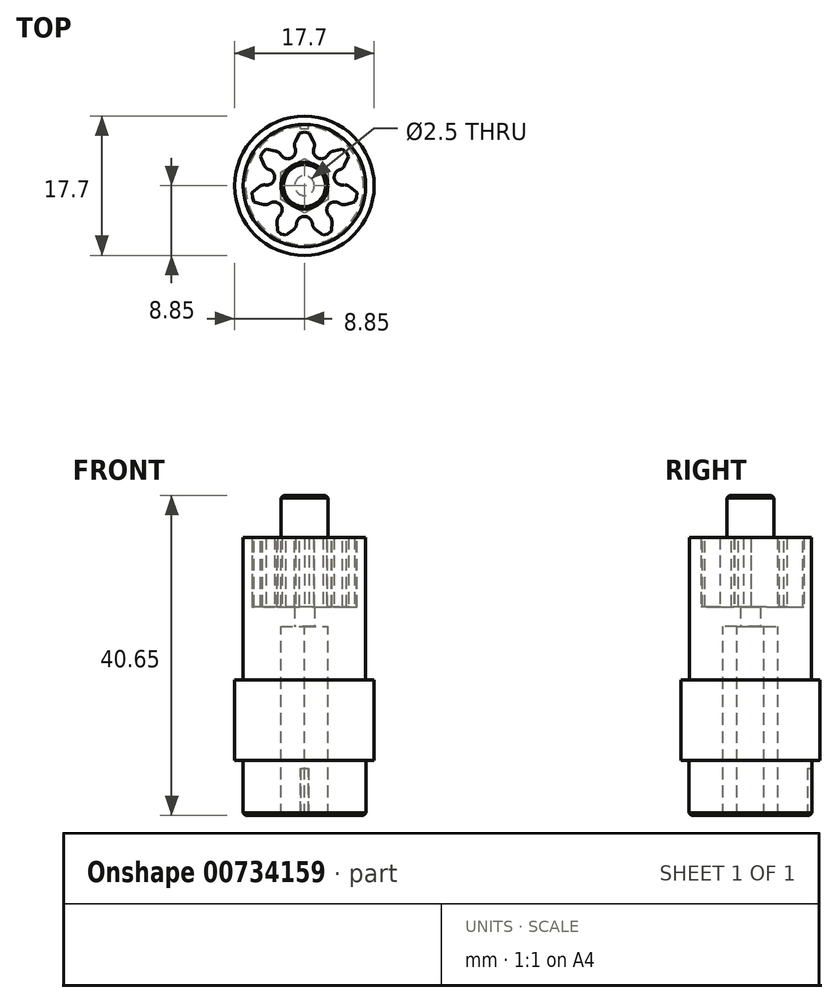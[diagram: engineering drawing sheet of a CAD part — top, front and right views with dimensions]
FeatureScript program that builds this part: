
annotation { "Feature Type Name" : "Feature", "Feature Type Description" : "" }
export const myFeature = defineFeature(function(context is Context, id is Id, definition is map)
    precondition{}
    {
        {
            var Q0;
            Q0=qCreatedBy(makeId("Top.planeOp"),FACE);
            var sketch = newSketch(context, id + "F0", { "sketchPlane" : qUnion([Q0])});
            skCircle(sketch, "E0", {"center": v(0, 0) * mm, "radius": 7.77 * mm});
            skCircle(sketch, "E1.cCircle", {"center": v(0, 0) * mm, "radius": 3 * mm, "construction": true});
            skLineSegment(sketch, "E1.0", {"start": v(0, 3.46) * mm, "end": v(3, 1.73) * mm});
            skLineSegment(sketch, "E1.1", {"start": v(3, 1.73) * mm, "end": v(3, -1.73) * mm});
            skLineSegment(sketch, "E1.2", {"start": v(3, -1.73) * mm, "end": v(0, -3.46) * mm});
            skLineSegment(sketch, "E1.3", {"start": v(0, -3.46) * mm, "end": v(-3, -1.73) * mm});
            skLineSegment(sketch, "E1.4", {"start": v(-3, -1.73) * mm, "end": v(-3, 1.73) * mm});
            skLineSegment(sketch, "E1.5", {"start": v(-3, 1.73) * mm, "end": v(0, 3.46) * mm});
            skPoint(sketch, "E1.0.midPoint", {"position": v(1.5, 2.6) * mm});
            skCircle(sketch, "E2", {"center": v(0, 0) * mm, "radius": 1.25 * mm});
            skSolve(sketch);
        }
        {
            var Q0;
            Q0=makeQuery(id+"F0.imprint","IMPRINT",FACE,{"disambiguationData":[TD([[makeQuery(id+"F0.imprint","IMPRINT",EDGE,{"derivedFrom":sQuery(id+"F0.wireOp",EDGE,"E1.0")}),-1.0]])]});
            var Q1;
            Q1=makeQuery(id+"F0.imprint","IMPRINT",FACE,{"disambiguationData":[TD([[makeQuery(id+"F0.imprint","IMPRINT",EDGE,{"derivedFrom":sQuery(id+"F0.wireOp",EDGE,"E0")}),1.0]])]});
            extrude(context, id + "F1", {"entities" : qUnion([Q0, Q1]), "depth" : 2.5 * mm, "offsetDistance" : 25 * mm});
        }
        {
            var Q0;
            Q0=makeQuery(id+"F0.imprint","IMPRINT",FACE,{"disambiguationData":[TD([[makeQuery(id+"F0.imprint","IMPRINT",EDGE,{"derivedFrom":sQuery(id+"F0.wireOp",EDGE,"E0")}),1.0]])]});
            extrude(context, id + "F2", {"entities" : qUnion([Q0]), "operationType" : NewBodyOperationType.ADD, "oppositeDirection" : true, "depth" : 6.8 * mm, "offsetDistance" : 25 * mm});
        }
        {
            var Q0;
            Q0=makeQuery(id+"F2.opExtrude","CAP_FACE",FACE,{"disambiguationData":[OSD([sQuery(id+"F0.wireOp",EDGE,"E0"),sQuery(id+"F0.wireOp",EDGE,"E1.0"),sQuery(id+"F0.wireOp",EDGE,"E1.1"),sQuery(id+"F0.wireOp",EDGE,"E1.2"),sQuery(id+"F0.wireOp",EDGE,"E1.3"),sQuery(id+"F0.wireOp",EDGE,"E1.4"),sQuery(id+"F0.wireOp",EDGE,"E1.5")])],"isStart":false});
            var sketch = newSketch(context, id + "F3", { "sketchPlane" : qUnion([Q0])});
            skCircle(sketch, "E3", {"center": v(0, 0) * mm, "radius": 8.85 * mm});
            skSolve(sketch);
        }
        {
            var Q0;
            Q0=makeQuery(id+"F3.imprint","IMPRINT",FACE,{"disambiguationData":[TD([[makeQuery(id+"F3.imprint","IMPRINT",EDGE,{"derivedFrom":makeQuery(id+"F2.opExtrude","CAP_EDGE",EDGE,{"disambiguationData":[OSD([sQuery(id+"F0.wireOp",EDGE,"E0")])],"isStart":false})}),-1.0]])]});
            var Q1;
            Q1=makeQuery(id+"F3.imprint","IMPRINT",FACE,{"disambiguationData":[TD([[makeQuery(id+"F3.imprint","IMPRINT",EDGE,{"derivedFrom":sQuery(id+"F3.wireOp",EDGE,"E3")}),1.0]])]});
            extrude(context, id + "F4", {"entities" : qUnion([Q0, Q1]), "operationType" : NewBodyOperationType.ADD, "depth" : 1.5 * mm, "offsetDistance" : 25 * mm});
        }
        {
            var Q0;
            Q0=makeQuery(id+"F4.opExtrude","CAP_FACE",FACE,{"disambiguationData":[OSD([sQuery(id+"F0.wireOp",EDGE,"E1.0"),sQuery(id+"F0.wireOp",EDGE,"E1.1"),sQuery(id+"F0.wireOp",EDGE,"E1.2"),sQuery(id+"F0.wireOp",EDGE,"E1.3"),sQuery(id+"F0.wireOp",EDGE,"E1.4"),sQuery(id+"F0.wireOp",EDGE,"E1.5"),sQuery(id+"F3.wireOp",EDGE,"E3")])],"isStart":false});
            var sketch = newSketch(context, id + "F5", { "sketchPlane" : qUnion([Q0])});
            skCircle(sketch, "E4", {"center": v(0, 0) * mm, "radius": 16.2 * mm, "construction": true});
            skLineSegment(sketch, "E5", {"start": v(0, 0) * mm, "end": v(0, 17.55) * mm, "construction": true});
            skCircle(sketch, "E6", {"center": v(0, 0) * mm, "radius": 15.75 * mm, "construction": true});
            skCircle(sketch, "E7", {"center": v(0, 0) * mm, "radius": 17.55 * mm, "construction": true});
            skArc(sketch, "E8", {"start": v(-0.72, 16.18) * mm, "mid": v(-1.14, 15.7) * mm, "end": v(-1.62, 16.12) * mm});
            skArc(sketch, "E9", {"start": v(-0.3, 17.55) * mm, "mid": v(-0.15, 17.55) * mm, "end": v(0, 17.55) * mm});
            skLineSegment(sketch, "E10", {"start": v(-0.72, 16.18) * mm, "end": v(-0.74, 16.43) * mm});
            skLineSegment(sketch, "E11", {"start": v(-0.74, 16.43) * mm, "end": v(-0.3, 17.55) * mm});
            skArc(sketch, "E12.MirrorCS", {"start": v(0.3, 17.55) * mm, "mid": v(0.15, 17.55) * mm, "end": v(0, 17.55) * mm});
            skLineSegment(sketch, "E13.MirrorCS", {"start": v(0.74, 16.43) * mm, "end": v(0.3, 17.55) * mm});
            skLineSegment(sketch, "E14.MirrorCS", {"start": v(0.72, 16.18) * mm, "end": v(0.74, 16.43) * mm});
            skArc(sketch, "E15.1.0", {"start": v(-2.24, 17.4) * mm, "mid": v(-2.39, 17.39) * mm, "end": v(-2.53, 17.37) * mm});
            skArc(sketch, "E15.1.1", {"start": v(-2.83, 17.32) * mm, "mid": v(-2.68, 17.34) * mm, "end": v(-2.53, 17.37) * mm});
            skLineSegment(sketch, "E15.1.2", {"start": v(-1.64, 16.37) * mm, "end": v(-2.24, 17.4) * mm});
            skLineSegment(sketch, "E15.1.3", {"start": v(-1.62, 16.12) * mm, "end": v(-1.64, 16.37) * mm});
            skLineSegment(sketch, "E15.1.4", {"start": v(-3.1, 16.15) * mm, "end": v(-2.83, 17.32) * mm});
            skLineSegment(sketch, "E15.1.5", {"start": v(-3.05, 15.9) * mm, "end": v(-3.1, 16.15) * mm});
            skArc(sketch, "E15.1.6", {"start": v(-3.05, 15.9) * mm, "mid": v(-3.4, 15.38) * mm, "end": v(-3.93, 15.71) * mm});
            skArc(sketch, "E15.2.0", {"start": v(-4.73, 16.9) * mm, "mid": v(-4.87, 16.86) * mm, "end": v(-5.01, 16.81) * mm});
            skArc(sketch, "E15.2.1", {"start": v(-5.3, 16.72) * mm, "mid": v(-5.16, 16.77) * mm, "end": v(-5.01, 16.81) * mm});
            skLineSegment(sketch, "E15.2.2", {"start": v(-3.99, 15.96) * mm, "end": v(-4.73, 16.9) * mm});
            skLineSegment(sketch, "E15.2.3", {"start": v(-3.93, 15.71) * mm, "end": v(-3.99, 15.96) * mm});
            skLineSegment(sketch, "E15.2.4", {"start": v(-5.4, 15.53) * mm, "end": v(-5.3, 16.72) * mm});
            skLineSegment(sketch, "E15.2.5", {"start": v(-5.31, 15.3) * mm, "end": v(-5.4, 15.53) * mm});
            skArc(sketch, "E15.2.6", {"start": v(-5.31, 15.3) * mm, "mid": v(-5.57, 14.72) * mm, "end": v(-6.15, 14.98) * mm});
            skArc(sketch, "E15.3.0", {"start": v(-7.11, 16.03) * mm, "mid": v(-7.25, 15.97) * mm, "end": v(-7.39, 15.9) * mm});
            skArc(sketch, "E15.3.1", {"start": v(-7.66, 15.78) * mm, "mid": v(-7.52, 15.84) * mm, "end": v(-7.39, 15.9) * mm});
            skLineSegment(sketch, "E15.3.2", {"start": v(-6.24, 15.2) * mm, "end": v(-7.11, 16.03) * mm});
            skLineSegment(sketch, "E15.3.3", {"start": v(-6.15, 14.98) * mm, "end": v(-6.24, 15.2) * mm});
            skLineSegment(sketch, "E15.3.4", {"start": v(-7.58, 14.58) * mm, "end": v(-7.66, 15.78) * mm});
            skLineSegment(sketch, "E15.3.5", {"start": v(-7.46, 14.36) * mm, "end": v(-7.58, 14.58) * mm});
            skArc(sketch, "E15.3.6", {"start": v(-7.46, 14.36) * mm, "mid": v(-7.64, 13.76) * mm, "end": v(-8.25, 13.92) * mm});
            skArc(sketch, "E15.4.0", {"start": v(-9.35, 14.83) * mm, "mid": v(-9.48, 14.75) * mm, "end": v(-9.6, 14.66) * mm});
            skArc(sketch, "E15.4.1", {"start": v(-9.85, 14.5) * mm, "mid": v(-9.73, 14.58) * mm, "end": v(-9.6, 14.66) * mm});
            skLineSegment(sketch, "E15.4.2", {"start": v(-8.37, 14.14) * mm, "end": v(-9.35, 14.83) * mm});
            skLineSegment(sketch, "E15.4.3", {"start": v(-8.25, 13.92) * mm, "end": v(-8.37, 14.14) * mm});
            skLineSegment(sketch, "E15.4.4", {"start": v(-9.6, 13.33) * mm, "end": v(-9.85, 14.5) * mm});
            skLineSegment(sketch, "E15.4.5", {"start": v(-9.45, 13.13) * mm, "end": v(-9.6, 13.33) * mm});
            skArc(sketch, "E15.4.6", {"start": v(-9.45, 13.13) * mm, "mid": v(-9.54, 12.5) * mm, "end": v(-10.16, 12.58) * mm});
            skArc(sketch, "E15.5.0", {"start": v(-11.39, 13.3) * mm, "mid": v(-11.5, 13.21) * mm, "end": v(-11.61, 13.11) * mm});
            skArc(sketch, "E15.5.1", {"start": v(-11.83, 12.9) * mm, "mid": v(-11.72, 13.01) * mm, "end": v(-11.61, 13.11) * mm});
            skLineSegment(sketch, "E15.5.2", {"start": v(-10.32, 12.77) * mm, "end": v(-11.39, 13.3) * mm});
            skLineSegment(sketch, "E15.5.3", {"start": v(-10.16, 12.58) * mm, "end": v(-10.32, 12.77) * mm});
            skLineSegment(sketch, "E15.5.4", {"start": v(-11.42, 11.79) * mm, "end": v(-11.83, 12.9) * mm});
            skLineSegment(sketch, "E15.5.5", {"start": v(-11.24, 11.61) * mm, "end": v(-11.42, 11.79) * mm});
            skArc(sketch, "E15.5.6", {"start": v(-11.24, 11.61) * mm, "mid": v(-11.23, 10.98) * mm, "end": v(-11.86, 10.96) * mm});
            skArc(sketch, "E15.6.0", {"start": v(-13.18, 11.51) * mm, "mid": v(-13.28, 11.4) * mm, "end": v(-13.38, 11.28) * mm});
            skArc(sketch, "E15.6.1", {"start": v(-13.57, 11.05) * mm, "mid": v(-13.47, 11.17) * mm, "end": v(-13.38, 11.28) * mm});
            skLineSegment(sketch, "E15.6.2", {"start": v(-12.05, 11.14) * mm, "end": v(-13.18, 11.51) * mm});
            skLineSegment(sketch, "E15.6.3", {"start": v(-11.86, 10.96) * mm, "end": v(-12.05, 11.14) * mm});
            skLineSegment(sketch, "E15.6.4", {"start": v(-12.99, 10) * mm, "end": v(-13.57, 11.05) * mm});
            skLineSegment(sketch, "E15.6.5", {"start": v(-12.79, 9.85) * mm, "end": v(-12.99, 10) * mm});
            skArc(sketch, "E15.6.6", {"start": v(-12.79, 9.85) * mm, "mid": v(-12.69, 9.23) * mm, "end": v(-13.31, 9.12) * mm});
            skArc(sketch, "E15.7.0", {"start": v(-14.7, 9.47) * mm, "mid": v(-14.78, 9.35) * mm, "end": v(-14.85, 9.22) * mm});
            skArc(sketch, "E15.7.1", {"start": v(-15, 8.96) * mm, "mid": v(-14.93, 9.09) * mm, "end": v(-14.85, 9.22) * mm});
            skLineSegment(sketch, "E15.7.2", {"start": v(-13.52, 9.27) * mm, "end": v(-14.7, 9.47) * mm});
            skLineSegment(sketch, "E15.7.3", {"start": v(-13.31, 9.12) * mm, "end": v(-13.52, 9.27) * mm});
            skLineSegment(sketch, "E15.7.4", {"start": v(-14.29, 8) * mm, "end": v(-15, 8.96) * mm});
            skLineSegment(sketch, "E15.7.5", {"start": v(-14.07, 7.89) * mm, "end": v(-14.29, 8) * mm});
            skArc(sketch, "E15.7.6", {"start": v(-14.07, 7.89) * mm, "mid": v(-13.88, 7.29) * mm, "end": v(-14.48, 7.09) * mm});
            skArc(sketch, "E15.8.0", {"start": v(-15.9, 7.23) * mm, "mid": v(-15.96, 7.1) * mm, "end": v(-16.02, 6.96) * mm});
            skArc(sketch, "E15.8.1", {"start": v(-16.13, 6.68) * mm, "mid": v(-16.08, 6.82) * mm, "end": v(-16.02, 6.96) * mm});
            skLineSegment(sketch, "E15.8.2", {"start": v(-14.7, 7.2) * mm, "end": v(-15.9, 7.23) * mm});
            skLineSegment(sketch, "E15.8.3", {"start": v(-14.48, 7.09) * mm, "end": v(-14.7, 7.2) * mm});
            skLineSegment(sketch, "E15.8.4", {"start": v(-15.28, 5.84) * mm, "end": v(-16.13, 6.68) * mm});
            skLineSegment(sketch, "E15.8.5", {"start": v(-15.04, 5.76) * mm, "end": v(-15.28, 5.84) * mm});
            skArc(sketch, "E15.8.6", {"start": v(-15.04, 5.76) * mm, "mid": v(-14.77, 5.2) * mm, "end": v(-15.33, 4.9) * mm});
            skArc(sketch, "E15.9.0", {"start": v(-16.76, 4.84) * mm, "mid": v(-16.8, 4.7) * mm, "end": v(-16.84, 4.55) * mm});
            skArc(sketch, "E15.9.1", {"start": v(-16.91, 4.26) * mm, "mid": v(-16.88, 4.4) * mm, "end": v(-16.84, 4.55) * mm});
            skLineSegment(sketch, "E15.9.2", {"start": v(-15.57, 4.99) * mm, "end": v(-16.76, 4.84) * mm});
            skLineSegment(sketch, "E15.9.3", {"start": v(-15.33, 4.9) * mm, "end": v(-15.57, 4.99) * mm});
            skLineSegment(sketch, "E15.9.4", {"start": v(-15.94, 3.56) * mm, "end": v(-16.91, 4.26) * mm});
            skLineSegment(sketch, "E15.9.5", {"start": v(-15.7, 3.51) * mm, "end": v(-15.94, 3.56) * mm});
            skArc(sketch, "E15.9.6", {"start": v(-15.7, 3.51) * mm, "mid": v(-15.34, 2.99) * mm, "end": v(-15.86, 2.63) * mm});
            skArc(sketch, "E15.10.0", {"start": v(-17.26, 2.35) * mm, "mid": v(-17.28, 2.2) * mm, "end": v(-17.3, 2.06) * mm});
            skArc(sketch, "E15.10.1", {"start": v(-17.33, 1.76) * mm, "mid": v(-17.32, 1.9) * mm, "end": v(-17.3, 2.06) * mm});
            skLineSegment(sketch, "E15.10.2", {"start": v(-16.1, 2.67) * mm, "end": v(-17.26, 2.35) * mm});
            skLineSegment(sketch, "E15.10.3", {"start": v(-15.86, 2.63) * mm, "end": v(-16.1, 2.67) * mm});
            skLineSegment(sketch, "E15.10.4", {"start": v(-16.27, 1.2) * mm, "end": v(-17.33, 1.76) * mm});
            skLineSegment(sketch, "E15.10.5", {"start": v(-16.02, 1.19) * mm, "end": v(-16.27, 1.2) * mm});
            skArc(sketch, "E15.10.6", {"start": v(-16.02, 1.19) * mm, "mid": v(-15.6, 0.72) * mm, "end": v(-16.05, 0.29) * mm});
            skArc(sketch, "E15.11.0", {"start": v(-17.4, -0.18) * mm, "mid": v(-17.4, -0.33) * mm, "end": v(-17.4, -0.48) * mm});
            skArc(sketch, "E15.11.1", {"start": v(-17.38, -0.78) * mm, "mid": v(-17.39, -0.63) * mm, "end": v(-17.4, -0.48) * mm});
            skLineSegment(sketch, "E15.11.2", {"start": v(-16.3, 0.3) * mm, "end": v(-17.4, -0.18) * mm});
            skLineSegment(sketch, "E15.11.3", {"start": v(-16.05, 0.29) * mm, "end": v(-16.3, 0.3) * mm});
            skLineSegment(sketch, "E15.11.4", {"start": v(-16.25, -1.18) * mm, "end": v(-17.38, -0.78) * mm});
            skLineSegment(sketch, "E15.11.5", {"start": v(-16, -1.15) * mm, "end": v(-16.25, -1.18) * mm});
            skArc(sketch, "E15.11.6", {"start": v(-16, -1.15) * mm, "mid": v(-15.51, -1.55) * mm, "end": v(-15.9, -2.05) * mm});
            skArc(sketch, "E15.12.0", {"start": v(-17.17, -2.71) * mm, "mid": v(-17.14, -2.86) * mm, "end": v(-17.12, -3) * mm});
            skArc(sketch, "E15.12.1", {"start": v(-17.06, -3.3) * mm, "mid": v(-17.09, -3.15) * mm, "end": v(-17.12, -3) * mm});
            skLineSegment(sketch, "E15.12.2", {"start": v(-16.15, -2.08) * mm, "end": v(-17.17, -2.71) * mm});
            skLineSegment(sketch, "E15.12.3", {"start": v(-15.9, -2.05) * mm, "end": v(-16.15, -2.08) * mm});
            skLineSegment(sketch, "E15.12.4", {"start": v(-15.88, -3.53) * mm, "end": v(-17.06, -3.3) * mm});
            skLineSegment(sketch, "E15.12.5", {"start": v(-15.64, -3.47) * mm, "end": v(-15.88, -3.53) * mm});
            skArc(sketch, "E15.12.6", {"start": v(-15.64, -3.47) * mm, "mid": v(-15.1, -3.8) * mm, "end": v(-15.41, -4.34) * mm});
            skArc(sketch, "E15.13.0", {"start": v(-16.57, -5.18) * mm, "mid": v(-16.52, -5.32) * mm, "end": v(-16.47, -5.46) * mm});
            skArc(sketch, "E15.13.1", {"start": v(-16.37, -5.75) * mm, "mid": v(-16.43, -5.6) * mm, "end": v(-16.47, -5.46) * mm});
            skLineSegment(sketch, "E15.13.2", {"start": v(-15.66, -4.4) * mm, "end": v(-16.57, -5.18) * mm});
            skLineSegment(sketch, "E15.13.3", {"start": v(-15.41, -4.34) * mm, "end": v(-15.66, -4.4) * mm});
            skLineSegment(sketch, "E15.13.4", {"start": v(-15.18, -5.8) * mm, "end": v(-16.37, -5.75) * mm});
            skLineSegment(sketch, "E15.13.5", {"start": v(-14.95, -5.7) * mm, "end": v(-15.18, -5.8) * mm});
            skArc(sketch, "E15.13.6", {"start": v(-14.95, -5.7) * mm, "mid": v(-14.36, -5.95) * mm, "end": v(-14.6, -6.54) * mm});
            skArc(sketch, "E15.14.0", {"start": v(-15.62, -7.54) * mm, "mid": v(-15.55, -7.67) * mm, "end": v(-15.48, -7.8) * mm});
            skArc(sketch, "E15.14.1", {"start": v(-15.34, -8.07) * mm, "mid": v(-15.41, -7.94) * mm, "end": v(-15.48, -7.8) * mm});
            skLineSegment(sketch, "E15.14.2", {"start": v(-14.83, -6.64) * mm, "end": v(-15.62, -7.54) * mm});
            skLineSegment(sketch, "E15.14.3", {"start": v(-14.6, -6.54) * mm, "end": v(-14.83, -6.64) * mm});
            skLineSegment(sketch, "E15.14.4", {"start": v(-14.15, -7.95) * mm, "end": v(-15.34, -8.07) * mm});
            skLineSegment(sketch, "E15.14.5", {"start": v(-13.94, -7.82) * mm, "end": v(-14.15, -7.95) * mm});
            skArc(sketch, "E15.14.6", {"start": v(-13.94, -7.82) * mm, "mid": v(-13.32, -7.97) * mm, "end": v(-13.47, -8.59) * mm});
            skArc(sketch, "E15.15.0", {"start": v(-14.33, -9.73) * mm, "mid": v(-14.25, -9.85) * mm, "end": v(-14.16, -9.97) * mm});
            skArc(sketch, "E15.15.1", {"start": v(-13.98, -10.21) * mm, "mid": v(-14.07, -10.1) * mm, "end": v(-14.16, -9.97) * mm});
            skLineSegment(sketch, "E15.15.2", {"start": v(-13.68, -8.72) * mm, "end": v(-14.33, -9.73) * mm});
            skLineSegment(sketch, "E15.15.3", {"start": v(-13.47, -8.59) * mm, "end": v(-13.68, -8.72) * mm});
            skLineSegment(sketch, "E15.15.4", {"start": v(-12.82, -9.92) * mm, "end": v(-13.98, -10.21) * mm});
            skLineSegment(sketch, "E15.15.5", {"start": v(-12.63, -9.76) * mm, "end": v(-12.82, -9.92) * mm});
            skArc(sketch, "E15.15.6", {"start": v(-12.63, -9.76) * mm, "mid": v(-12, -9.83) * mm, "end": v(-12.05, -10.46) * mm});
            skArc(sketch, "E15.16.0", {"start": v(-12.74, -11.7) * mm, "mid": v(-12.64, -11.82) * mm, "end": v(-12.53, -11.92) * mm});
            skArc(sketch, "E15.16.1", {"start": v(-12.32, -12.14) * mm, "mid": v(-12.43, -12.03) * mm, "end": v(-12.53, -11.92) * mm});
            skLineSegment(sketch, "E15.16.2", {"start": v(-12.24, -10.62) * mm, "end": v(-12.74, -11.7) * mm});
            skLineSegment(sketch, "E15.16.3", {"start": v(-12.05, -10.46) * mm, "end": v(-12.24, -10.62) * mm});
            skLineSegment(sketch, "E15.16.4", {"start": v(-11.22, -11.68) * mm, "end": v(-12.32, -12.14) * mm});
            skLineSegment(sketch, "E15.16.5", {"start": v(-11.05, -11.5) * mm, "end": v(-11.22, -11.68) * mm});
            skArc(sketch, "E15.16.6", {"start": v(-11.05, -11.5) * mm, "mid": v(-10.42, -11.47) * mm, "end": v(-10.38, -12.1) * mm});
            skArc(sketch, "E15.17.0", {"start": v(-10.88, -13.44) * mm, "mid": v(-10.76, -13.53) * mm, "end": v(-10.64, -13.62) * mm});
            skArc(sketch, "E15.17.1", {"start": v(-10.4, -13.8) * mm, "mid": v(-10.52, -13.71) * mm, "end": v(-10.64, -13.62) * mm});
            skLineSegment(sketch, "E15.17.2", {"start": v(-10.54, -12.29) * mm, "end": v(-10.88, -13.44) * mm});
            skLineSegment(sketch, "E15.17.3", {"start": v(-10.38, -12.1) * mm, "end": v(-10.54, -12.29) * mm});
            skLineSegment(sketch, "E15.17.4", {"start": v(-9.38, -13.19) * mm, "end": v(-10.4, -13.8) * mm});
            skLineSegment(sketch, "E15.17.5", {"start": v(-9.24, -12.98) * mm, "end": v(-9.38, -13.19) * mm});
            skArc(sketch, "E15.17.6", {"start": v(-9.24, -12.98) * mm, "mid": v(-8.62, -12.86) * mm, "end": v(-8.49, -13.48) * mm});
            skArc(sketch, "E15.18.0", {"start": v(-8.78, -14.87) * mm, "mid": v(-8.65, -14.95) * mm, "end": v(-8.52, -15.02) * mm});
            skArc(sketch, "E15.18.1", {"start": v(-8.26, -15.17) * mm, "mid": v(-8.4, -15.1) * mm, "end": v(-8.52, -15.02) * mm});
            skLineSegment(sketch, "E15.18.2", {"start": v(-8.62, -13.69) * mm, "end": v(-8.78, -14.87) * mm});
            skLineSegment(sketch, "E15.18.3", {"start": v(-8.49, -13.48) * mm, "end": v(-8.62, -13.69) * mm});
            skLineSegment(sketch, "E15.18.4", {"start": v(-7.33, -14.4) * mm, "end": v(-8.26, -15.17) * mm});
            skLineSegment(sketch, "E15.18.5", {"start": v(-7.23, -14.18) * mm, "end": v(-7.33, -14.4) * mm});
            skArc(sketch, "E15.18.6", {"start": v(-7.23, -14.18) * mm, "mid": v(-6.63, -13.97) * mm, "end": v(-6.41, -14.57) * mm});
            skArc(sketch, "E15.19.0", {"start": v(-6.5, -16) * mm, "mid": v(-6.36, -16.05) * mm, "end": v(-6.22, -16.1) * mm});
            skArc(sketch, "E15.19.1", {"start": v(-5.94, -16.2) * mm, "mid": v(-6.08, -16.15) * mm, "end": v(-6.22, -16.1) * mm});
            skLineSegment(sketch, "E15.19.2", {"start": v(-6.51, -14.8) * mm, "end": v(-6.5, -16) * mm});
            skLineSegment(sketch, "E15.19.3", {"start": v(-6.41, -14.57) * mm, "end": v(-6.51, -14.8) * mm});
            skLineSegment(sketch, "E15.19.4", {"start": v(-5.14, -15.32) * mm, "end": v(-5.94, -16.2) * mm});
            skLineSegment(sketch, "E15.19.5", {"start": v(-5.06, -15.08) * mm, "end": v(-5.14, -15.32) * mm});
            skArc(sketch, "E15.19.6", {"start": v(-5.06, -15.08) * mm, "mid": v(-4.5, -14.79) * mm, "end": v(-4.2, -15.34) * mm});
            skArc(sketch, "E15.20.0", {"start": v(-4.08, -16.77) * mm, "mid": v(-3.94, -16.8) * mm, "end": v(-3.8, -16.83) * mm});
            skArc(sketch, "E15.20.1", {"start": v(-3.5, -16.9) * mm, "mid": v(-3.65, -16.87) * mm, "end": v(-3.8, -16.83) * mm});
            skLineSegment(sketch, "E15.20.2", {"start": v(-4.27, -15.58) * mm, "end": v(-4.08, -16.77) * mm});
            skLineSegment(sketch, "E15.20.3", {"start": v(-4.2, -15.34) * mm, "end": v(-4.27, -15.58) * mm});
            skLineSegment(sketch, "E15.20.4", {"start": v(-2.83, -15.9) * mm, "end": v(-3.5, -16.9) * mm});
            skLineSegment(sketch, "E15.20.5", {"start": v(-2.79, -15.66) * mm, "end": v(-2.83, -15.9) * mm});
            skArc(sketch, "E15.20.6", {"start": v(-2.79, -15.66) * mm, "mid": v(-2.28, -15.28) * mm, "end": v(-1.9, -15.79) * mm});
            skArc(sketch, "E15.21.0", {"start": v(-1.58, -17.18) * mm, "mid": v(-1.43, -17.2) * mm, "end": v(-1.28, -17.2) * mm});
            skArc(sketch, "E15.21.1", {"start": v(-0.98, -17.22) * mm, "mid": v(-1.13, -17.21) * mm, "end": v(-1.28, -17.2) * mm});
            skLineSegment(sketch, "E15.21.2", {"start": v(-1.93, -16.04) * mm, "end": v(-1.58, -17.18) * mm});
            skLineSegment(sketch, "E15.21.3", {"start": v(-1.9, -15.79) * mm, "end": v(-1.93, -16.04) * mm});
            skLineSegment(sketch, "E15.21.4", {"start": v(-0.46, -16.14) * mm, "end": v(-0.98, -17.22) * mm});
            skLineSegment(sketch, "E15.21.5", {"start": v(-0.46, -15.9) * mm, "end": v(-0.46, -16.14) * mm});
            skArc(sketch, "E15.21.6", {"start": v(-0.46, -15.9) * mm, "mid": v(0, -15.45) * mm, "end": v(0.44, -15.9) * mm});
            skArc(sketch, "E15.22.0", {"start": v(0.96, -17.22) * mm, "mid": v(1.11, -17.22) * mm, "end": v(1.26, -17.2) * mm});
            skArc(sketch, "E15.22.1", {"start": v(1.56, -17.18) * mm, "mid": v(1.41, -17.2) * mm, "end": v(1.26, -17.2) * mm});
            skLineSegment(sketch, "E15.22.2", {"start": v(0.45, -16.15) * mm, "end": v(0.96, -17.22) * mm});
            skLineSegment(sketch, "E15.22.3", {"start": v(0.44, -15.9) * mm, "end": v(0.45, -16.15) * mm});
            skLineSegment(sketch, "E15.22.4", {"start": v(1.92, -16.04) * mm, "end": v(1.56, -17.18) * mm});
            skLineSegment(sketch, "E15.22.5", {"start": v(1.88, -15.79) * mm, "end": v(1.92, -16.04) * mm});
            skArc(sketch, "E15.22.6", {"start": v(1.88, -15.79) * mm, "mid": v(2.26, -15.29) * mm, "end": v(2.77, -15.66) * mm});
            skArc(sketch, "E15.23.0", {"start": v(3.48, -16.9) * mm, "mid": v(3.63, -16.87) * mm, "end": v(3.78, -16.84) * mm});
            skArc(sketch, "E15.23.1", {"start": v(4.07, -16.77) * mm, "mid": v(3.92, -16.8) * mm, "end": v(3.78, -16.84) * mm});
            skLineSegment(sketch, "E15.23.2", {"start": v(2.81, -15.9) * mm, "end": v(3.48, -16.9) * mm});
            skLineSegment(sketch, "E15.23.3", {"start": v(2.77, -15.66) * mm, "end": v(2.81, -15.9) * mm});
            skLineSegment(sketch, "E15.23.4", {"start": v(4.25, -15.59) * mm, "end": v(4.07, -16.77) * mm});
            skLineSegment(sketch, "E15.23.5", {"start": v(4.18, -15.35) * mm, "end": v(4.25, -15.59) * mm});
            skArc(sketch, "E15.23.6", {"start": v(4.18, -15.35) * mm, "mid": v(4.49, -14.8) * mm, "end": v(5.05, -15.09) * mm});
            skArc(sketch, "E15.24.0", {"start": v(5.93, -16.2) * mm, "mid": v(6.07, -16.16) * mm, "end": v(6.2, -16.1) * mm});
            skArc(sketch, "E15.24.1", {"start": v(6.49, -16) * mm, "mid": v(6.35, -16.05) * mm, "end": v(6.2, -16.1) * mm});
            skLineSegment(sketch, "E15.24.2", {"start": v(5.12, -15.32) * mm, "end": v(5.93, -16.2) * mm});
            skLineSegment(sketch, "E15.24.3", {"start": v(5.05, -15.09) * mm, "end": v(5.12, -15.32) * mm});
            skLineSegment(sketch, "E15.24.4", {"start": v(6.5, -14.8) * mm, "end": v(6.49, -16) * mm});
            skLineSegment(sketch, "E15.24.5", {"start": v(6.4, -14.57) * mm, "end": v(6.5, -14.8) * mm});
            skArc(sketch, "E15.24.6", {"start": v(6.4, -14.57) * mm, "mid": v(6.61, -13.98) * mm, "end": v(7.2, -14.19) * mm});
            skArc(sketch, "E15.25.0", {"start": v(8.25, -15.17) * mm, "mid": v(8.38, -15.1) * mm, "end": v(8.5, -15.03) * mm});
            skArc(sketch, "E15.25.1", {"start": v(8.77, -14.88) * mm, "mid": v(8.64, -14.95) * mm, "end": v(8.5, -15.03) * mm});
            skLineSegment(sketch, "E15.25.2", {"start": v(7.32, -14.41) * mm, "end": v(8.25, -15.17) * mm});
            skLineSegment(sketch, "E15.25.3", {"start": v(7.2, -14.19) * mm, "end": v(7.32, -14.41) * mm});
            skLineSegment(sketch, "E15.25.4", {"start": v(8.6, -13.7) * mm, "end": v(8.77, -14.88) * mm});
            skLineSegment(sketch, "E15.25.5", {"start": v(8.47, -13.48) * mm, "end": v(8.6, -13.7) * mm});
            skArc(sketch, "E15.25.6", {"start": v(8.47, -13.48) * mm, "mid": v(8.6, -12.86) * mm, "end": v(9.22, -12.99) * mm});
            skArc(sketch, "E15.26.0", {"start": v(10.39, -13.8) * mm, "mid": v(10.5, -13.72) * mm, "end": v(10.63, -13.63) * mm});
            skArc(sketch, "E15.26.1", {"start": v(10.86, -13.44) * mm, "mid": v(10.75, -13.53) * mm, "end": v(10.63, -13.63) * mm});
            skLineSegment(sketch, "E15.26.2", {"start": v(9.36, -13.2) * mm, "end": v(10.39, -13.8) * mm});
            skLineSegment(sketch, "E15.26.3", {"start": v(9.22, -12.99) * mm, "end": v(9.36, -13.2) * mm});
            skLineSegment(sketch, "E15.26.4", {"start": v(10.53, -12.3) * mm, "end": v(10.86, -13.44) * mm});
            skLineSegment(sketch, "E15.26.5", {"start": v(10.36, -12.1) * mm, "end": v(10.53, -12.3) * mm});
            skArc(sketch, "E15.26.6", {"start": v(10.36, -12.1) * mm, "mid": v(10.4, -11.47) * mm, "end": v(11.03, -11.5) * mm});
            skArc(sketch, "E15.27.0", {"start": v(12.3, -12.15) * mm, "mid": v(12.42, -12.04) * mm, "end": v(12.52, -11.93) * mm});
            skArc(sketch, "E15.27.1", {"start": v(12.73, -11.71) * mm, "mid": v(12.62, -11.82) * mm, "end": v(12.52, -11.93) * mm});
            skLineSegment(sketch, "E15.27.2", {"start": v(11.2, -11.69) * mm, "end": v(12.3, -12.15) * mm});
            skLineSegment(sketch, "E15.27.3", {"start": v(11.03, -11.5) * mm, "end": v(11.2, -11.69) * mm});
            skLineSegment(sketch, "E15.27.4", {"start": v(12.23, -10.63) * mm, "end": v(12.73, -11.71) * mm});
            skLineSegment(sketch, "E15.27.5", {"start": v(12.04, -10.46) * mm, "end": v(12.23, -10.63) * mm});
            skArc(sketch, "E15.27.6", {"start": v(12.04, -10.46) * mm, "mid": v(11.98, -9.83) * mm, "end": v(12.61, -9.77) * mm});
            skArc(sketch, "E15.28.0", {"start": v(13.97, -10.22) * mm, "mid": v(14.06, -10.1) * mm, "end": v(14.15, -9.98) * mm});
            skArc(sketch, "E15.28.1", {"start": v(14.32, -9.73) * mm, "mid": v(14.23, -9.86) * mm, "end": v(14.15, -9.98) * mm});
            skLineSegment(sketch, "E15.28.2", {"start": v(12.8, -9.93) * mm, "end": v(13.97, -10.22) * mm});
            skLineSegment(sketch, "E15.28.3", {"start": v(12.61, -9.77) * mm, "end": v(12.8, -9.93) * mm});
            skLineSegment(sketch, "E15.28.4", {"start": v(13.67, -8.73) * mm, "end": v(14.32, -9.73) * mm});
            skLineSegment(sketch, "E15.28.5", {"start": v(13.45, -8.6) * mm, "end": v(13.67, -8.73) * mm});
            skArc(sketch, "E15.28.6", {"start": v(13.45, -8.6) * mm, "mid": v(13.31, -7.98) * mm, "end": v(13.92, -7.83) * mm});
            skArc(sketch, "E15.29.0", {"start": v(15.33, -8.08) * mm, "mid": v(15.4, -7.94) * mm, "end": v(15.47, -7.81) * mm});
            skArc(sketch, "E15.29.1", {"start": v(15.6, -7.54) * mm, "mid": v(15.54, -7.68) * mm, "end": v(15.47, -7.81) * mm});
            skLineSegment(sketch, "E15.29.2", {"start": v(14.14, -7.96) * mm, "end": v(15.33, -8.08) * mm});
            skLineSegment(sketch, "E15.29.3", {"start": v(13.92, -7.83) * mm, "end": v(14.14, -7.96) * mm});
            skLineSegment(sketch, "E15.29.4", {"start": v(14.81, -6.64) * mm, "end": v(15.6, -7.54) * mm});
            skLineSegment(sketch, "E15.29.5", {"start": v(14.58, -6.54) * mm, "end": v(14.81, -6.64) * mm});
            skArc(sketch, "E15.29.6", {"start": v(14.58, -6.54) * mm, "mid": v(14.35, -5.96) * mm, "end": v(14.94, -5.72) * mm});
            skArc(sketch, "E15.30.0", {"start": v(16.36, -5.76) * mm, "mid": v(16.41, -5.61) * mm, "end": v(16.46, -5.47) * mm});
            skArc(sketch, "E15.30.1", {"start": v(16.56, -5.19) * mm, "mid": v(16.51, -5.33) * mm, "end": v(16.46, -5.47) * mm});
            skLineSegment(sketch, "E15.30.2", {"start": v(15.17, -5.8) * mm, "end": v(16.36, -5.76) * mm});
            skLineSegment(sketch, "E15.30.3", {"start": v(14.94, -5.72) * mm, "end": v(15.17, -5.8) * mm});
            skLineSegment(sketch, "E15.30.4", {"start": v(15.64, -4.41) * mm, "end": v(16.56, -5.19) * mm});
            skLineSegment(sketch, "E15.30.5", {"start": v(15.4, -4.35) * mm, "end": v(15.64, -4.41) * mm});
            skArc(sketch, "E15.30.6", {"start": v(15.4, -4.35) * mm, "mid": v(15.09, -3.8) * mm, "end": v(15.63, -3.48) * mm});
            skArc(sketch, "E15.31.0", {"start": v(17.05, -3.3) * mm, "mid": v(17.08, -3.16) * mm, "end": v(17.1, -3.02) * mm});
            skArc(sketch, "E15.31.1", {"start": v(17.16, -2.72) * mm, "mid": v(17.13, -2.87) * mm, "end": v(17.1, -3.02) * mm});
            skLineSegment(sketch, "E15.31.2", {"start": v(15.87, -3.54) * mm, "end": v(17.05, -3.3) * mm});
            skLineSegment(sketch, "E15.31.3", {"start": v(15.63, -3.48) * mm, "end": v(15.87, -3.54) * mm});
            skLineSegment(sketch, "E15.31.4", {"start": v(16.14, -2.09) * mm, "end": v(17.16, -2.72) * mm});
            skLineSegment(sketch, "E15.31.5", {"start": v(15.9, -2.06) * mm, "end": v(16.14, -2.09) * mm});
            skArc(sketch, "E15.31.6", {"start": v(15.9, -2.06) * mm, "mid": v(15.5, -1.56) * mm, "end": v(16, -1.16) * mm});
            skArc(sketch, "E15.32.0", {"start": v(17.37, -0.79) * mm, "mid": v(17.38, -0.64) * mm, "end": v(17.38, -0.5) * mm});
            skArc(sketch, "E15.32.1", {"start": v(17.4, -0.2) * mm, "mid": v(17.39, -0.34) * mm, "end": v(17.38, -0.5) * mm});
            skLineSegment(sketch, "E15.32.2", {"start": v(16.24, -1.19) * mm, "end": v(17.37, -0.79) * mm});
            skLineSegment(sketch, "E15.32.3", {"start": v(16, -1.16) * mm, "end": v(16.24, -1.19) * mm});
            skLineSegment(sketch, "E15.32.4", {"start": v(16.3, 0.29) * mm, "end": v(17.4, -0.2) * mm});
            skLineSegment(sketch, "E15.32.5", {"start": v(16.05, 0.28) * mm, "end": v(16.3, 0.29) * mm});
            skArc(sketch, "E15.32.6", {"start": v(16.05, 0.28) * mm, "mid": v(15.59, 0.72) * mm, "end": v(16.01, 1.18) * mm});
            skArc(sketch, "E15.33.0", {"start": v(17.32, 1.75) * mm, "mid": v(17.3, 1.9) * mm, "end": v(17.3, 2.05) * mm});
            skArc(sketch, "E15.33.1", {"start": v(17.26, 2.35) * mm, "mid": v(17.28, 2.2) * mm, "end": v(17.3, 2.05) * mm});
            skLineSegment(sketch, "E15.33.2", {"start": v(16.26, 1.2) * mm, "end": v(17.32, 1.75) * mm});
            skLineSegment(sketch, "E15.33.3", {"start": v(16.01, 1.18) * mm, "end": v(16.26, 1.2) * mm});
            skLineSegment(sketch, "E15.33.4", {"start": v(16.1, 2.66) * mm, "end": v(17.26, 2.35) * mm});
            skLineSegment(sketch, "E15.33.5", {"start": v(15.86, 2.62) * mm, "end": v(16.1, 2.66) * mm});
            skArc(sketch, "E15.33.6", {"start": v(15.86, 2.62) * mm, "mid": v(15.34, 2.98) * mm, "end": v(15.7, 3.5) * mm});
            skArc(sketch, "E15.34.0", {"start": v(16.9, 4.26) * mm, "mid": v(16.87, 4.4) * mm, "end": v(16.83, 4.55) * mm});
            skArc(sketch, "E15.34.1", {"start": v(16.75, 4.84) * mm, "mid": v(16.8, 4.7) * mm, "end": v(16.83, 4.55) * mm});
            skLineSegment(sketch, "E15.34.2", {"start": v(15.94, 3.55) * mm, "end": v(16.9, 4.26) * mm});
            skLineSegment(sketch, "E15.34.3", {"start": v(15.7, 3.5) * mm, "end": v(15.94, 3.55) * mm});
            skLineSegment(sketch, "E15.34.4", {"start": v(15.56, 4.98) * mm, "end": v(16.75, 4.84) * mm});
            skLineSegment(sketch, "E15.34.5", {"start": v(15.33, 4.9) * mm, "end": v(15.56, 4.98) * mm});
            skArc(sketch, "E15.34.6", {"start": v(15.33, 4.9) * mm, "mid": v(14.76, 5.18) * mm, "end": v(15.04, 5.75) * mm});
            skArc(sketch, "E15.35.0", {"start": v(16.13, 6.67) * mm, "mid": v(16.07, 6.81) * mm, "end": v(16.01, 6.95) * mm});
            skArc(sketch, "E15.35.1", {"start": v(15.9, 7.23) * mm, "mid": v(15.95, 7.09) * mm, "end": v(16.01, 6.95) * mm});
            skLineSegment(sketch, "E15.35.2", {"start": v(15.27, 5.84) * mm, "end": v(16.13, 6.67) * mm});
            skLineSegment(sketch, "E15.35.3", {"start": v(15.04, 5.75) * mm, "end": v(15.27, 5.84) * mm});
            skLineSegment(sketch, "E15.35.4", {"start": v(14.7, 7.2) * mm, "end": v(15.9, 7.23) * mm});
            skLineSegment(sketch, "E15.35.5", {"start": v(14.47, 7.08) * mm, "end": v(14.7, 7.2) * mm});
            skArc(sketch, "E15.35.6", {"start": v(14.47, 7.08) * mm, "mid": v(13.87, 7.28) * mm, "end": v(14.06, 7.88) * mm});
            skArc(sketch, "E15.36.0", {"start": v(15, 8.95) * mm, "mid": v(14.93, 9.08) * mm, "end": v(14.85, 9.21) * mm});
            skArc(sketch, "E15.36.1", {"start": v(14.7, 9.47) * mm, "mid": v(14.77, 9.34) * mm, "end": v(14.85, 9.21) * mm});
            skLineSegment(sketch, "E15.36.2", {"start": v(14.28, 8) * mm, "end": v(15, 8.95) * mm});
            skLineSegment(sketch, "E15.36.3", {"start": v(14.06, 7.88) * mm, "end": v(14.28, 8) * mm});
            skLineSegment(sketch, "E15.36.4", {"start": v(13.51, 9.26) * mm, "end": v(14.7, 9.47) * mm});
            skLineSegment(sketch, "E15.36.5", {"start": v(13.3, 9.12) * mm, "end": v(13.51, 9.26) * mm});
            skArc(sketch, "E15.36.6", {"start": v(13.3, 9.12) * mm, "mid": v(12.69, 9.22) * mm, "end": v(12.79, 9.85) * mm});
            skArc(sketch, "E15.37.0", {"start": v(13.56, 11.04) * mm, "mid": v(13.47, 11.16) * mm, "end": v(13.37, 11.28) * mm});
            skArc(sketch, "E15.37.1", {"start": v(13.18, 11.5) * mm, "mid": v(13.28, 11.4) * mm, "end": v(13.37, 11.28) * mm});
            skLineSegment(sketch, "E15.37.2", {"start": v(12.99, 10) * mm, "end": v(13.56, 11.04) * mm});
            skLineSegment(sketch, "E15.37.3", {"start": v(12.79, 9.85) * mm, "end": v(12.99, 10) * mm});
            skLineSegment(sketch, "E15.37.4", {"start": v(12.04, 11.13) * mm, "end": v(13.18, 11.5) * mm});
            skLineSegment(sketch, "E15.37.5", {"start": v(11.86, 10.96) * mm, "end": v(12.04, 11.13) * mm});
            skArc(sketch, "E15.37.6", {"start": v(11.86, 10.96) * mm, "mid": v(11.23, 10.97) * mm, "end": v(11.24, 11.6) * mm});
            skArc(sketch, "E15.38.0", {"start": v(11.83, 12.9) * mm, "mid": v(11.72, 13) * mm, "end": v(11.61, 13.1) * mm});
            skArc(sketch, "E15.38.1", {"start": v(11.39, 13.3) * mm, "mid": v(11.5, 13.2) * mm, "end": v(11.61, 13.1) * mm});
            skLineSegment(sketch, "E15.38.2", {"start": v(11.41, 11.78) * mm, "end": v(11.83, 12.9) * mm});
            skLineSegment(sketch, "E15.38.3", {"start": v(11.24, 11.6) * mm, "end": v(11.41, 11.78) * mm});
            skLineSegment(sketch, "E15.38.4", {"start": v(10.32, 12.77) * mm, "end": v(11.39, 13.3) * mm});
            skLineSegment(sketch, "E15.38.5", {"start": v(10.16, 12.57) * mm, "end": v(10.32, 12.77) * mm});
            skArc(sketch, "E15.38.6", {"start": v(10.16, 12.57) * mm, "mid": v(9.53, 12.5) * mm, "end": v(9.45, 13.12) * mm});
            skArc(sketch, "E15.39.0", {"start": v(9.85, 14.5) * mm, "mid": v(9.73, 14.58) * mm, "end": v(9.6, 14.66) * mm});
            skArc(sketch, "E15.39.1", {"start": v(9.35, 14.82) * mm, "mid": v(9.47, 14.74) * mm, "end": v(9.6, 14.66) * mm});
            skLineSegment(sketch, "E15.39.2", {"start": v(9.6, 13.32) * mm, "end": v(9.85, 14.5) * mm});
            skLineSegment(sketch, "E15.39.3", {"start": v(9.45, 13.12) * mm, "end": v(9.6, 13.32) * mm});
            skLineSegment(sketch, "E15.39.4", {"start": v(8.37, 14.13) * mm, "end": v(9.35, 14.82) * mm});
            skLineSegment(sketch, "E15.39.5", {"start": v(8.24, 13.92) * mm, "end": v(8.37, 14.13) * mm});
            skArc(sketch, "E15.39.6", {"start": v(8.24, 13.92) * mm, "mid": v(7.63, 13.75) * mm, "end": v(7.46, 14.36) * mm});
            skArc(sketch, "E15.40.0", {"start": v(7.66, 15.77) * mm, "mid": v(7.52, 15.84) * mm, "end": v(7.39, 15.9) * mm});
            skArc(sketch, "E15.40.1", {"start": v(7.11, 16.03) * mm, "mid": v(7.25, 15.97) * mm, "end": v(7.39, 15.9) * mm});
            skLineSegment(sketch, "E15.40.2", {"start": v(7.58, 14.58) * mm, "end": v(7.66, 15.77) * mm});
            skLineSegment(sketch, "E15.40.3", {"start": v(7.46, 14.36) * mm, "end": v(7.58, 14.58) * mm});
            skLineSegment(sketch, "E15.40.4", {"start": v(6.24, 15.2) * mm, "end": v(7.11, 16.03) * mm});
            skLineSegment(sketch, "E15.40.5", {"start": v(6.15, 14.97) * mm, "end": v(6.24, 15.2) * mm});
            skArc(sketch, "E15.40.6", {"start": v(6.15, 14.97) * mm, "mid": v(5.57, 14.72) * mm, "end": v(5.31, 15.3) * mm});
            skArc(sketch, "E15.41.0", {"start": v(5.3, 16.72) * mm, "mid": v(5.16, 16.77) * mm, "end": v(5.01, 16.81) * mm});
            skArc(sketch, "E15.41.1", {"start": v(4.72, 16.9) * mm, "mid": v(4.87, 16.85) * mm, "end": v(5.01, 16.81) * mm});
            skLineSegment(sketch, "E15.41.2", {"start": v(5.4, 15.53) * mm, "end": v(5.3, 16.72) * mm});
            skLineSegment(sketch, "E15.41.3", {"start": v(5.31, 15.3) * mm, "end": v(5.4, 15.53) * mm});
            skLineSegment(sketch, "E15.41.4", {"start": v(3.99, 15.95) * mm, "end": v(4.72, 16.9) * mm});
            skLineSegment(sketch, "E15.41.5", {"start": v(3.93, 15.71) * mm, "end": v(3.99, 15.95) * mm});
            skArc(sketch, "E15.41.6", {"start": v(3.93, 15.71) * mm, "mid": v(3.4, 15.38) * mm, "end": v(3.05, 15.9) * mm});
            skArc(sketch, "E15.42.0", {"start": v(2.83, 17.32) * mm, "mid": v(2.68, 17.34) * mm, "end": v(2.53, 17.36) * mm});
            skArc(sketch, "E15.42.1", {"start": v(2.24, 17.4) * mm, "mid": v(2.38, 17.39) * mm, "end": v(2.53, 17.36) * mm});
            skLineSegment(sketch, "E15.42.2", {"start": v(3.1, 16.15) * mm, "end": v(2.83, 17.32) * mm});
            skLineSegment(sketch, "E15.42.3", {"start": v(3.05, 15.9) * mm, "end": v(3.1, 16.15) * mm});
            skLineSegment(sketch, "E15.42.4", {"start": v(1.64, 16.37) * mm, "end": v(2.24, 17.4) * mm});
            skLineSegment(sketch, "E15.42.5", {"start": v(1.62, 16.12) * mm, "end": v(1.64, 16.37) * mm});
            skArc(sketch, "E15.42.6", {"start": v(1.62, 16.12) * mm, "mid": v(1.14, 15.7) * mm, "end": v(0.72, 16.18) * mm});
            skPoint(sketch, "E15.center", {"position": v(0, 0.15) * mm});
            skSolve(sketch);
        }
        {
            var Q0;
            Q0=makeQuery(id+"F5.imprint","IMPRINT",FACE,{"disambiguationData":[TD([[makeQuery(id+"F5.imprint","IMPRINT",EDGE,{"derivedFrom":sQuery(id+"F5.wireOp",EDGE,"E8")}),1.0]])]});
            var Q1;
            Q1=makeQuery(id+"F5.imprint","IMPRINT",FACE,{"disambiguationData":[TD([[makeQuery(id+"F5.imprint","IMPRINT",EDGE,{"derivedFrom":makeQuery(id+"F4.opExtrude","CAP_EDGE",EDGE,{"disambiguationData":[OSD([sQuery(id+"F3.wireOp",EDGE,"E3")])],"isStart":false})}),1.0]])]});
            extrude(context, id + "F6", {"entities" : qUnion([Q0, Q1]), "operationType" : NewBodyOperationType.ADD, "depth" : 3.5 * mm, "offsetDistance" : 25 * mm});
        }
        {
            var Q0;
            Q0=makeQuery(id+"F6.opExtrude","CAP_FACE",FACE,{"disambiguationData":[OSD([sQuery(id+"F0.wireOp",EDGE,"E1.0"),sQuery(id+"F0.wireOp",EDGE,"E1.1"),sQuery(id+"F0.wireOp",EDGE,"E1.2"),sQuery(id+"F0.wireOp",EDGE,"E1.3"),sQuery(id+"F0.wireOp",EDGE,"E1.4"),sQuery(id+"F0.wireOp",EDGE,"E1.5"),sQuery(id+"F5.wireOp",EDGE,"E8"),sQuery(id+"F5.wireOp",EDGE,"E9"),sQuery(id+"F5.wireOp",EDGE,"E10"),sQuery(id+"F5.wireOp",EDGE,"E11"),sQuery(id+"F5.wireOp",EDGE,"E12.MirrorCS"),sQuery(id+"F5.wireOp",EDGE,"E13.MirrorCS"),sQuery(id+"F5.wireOp",EDGE,"E14.MirrorCS"),sQuery(id+"F5.wireOp",EDGE,"E15.1.0"),sQuery(id+"F5.wireOp",EDGE,"E15.1.1"),sQuery(id+"F5.wireOp",EDGE,"E15.1.2"),sQuery(id+"F5.wireOp",EDGE,"E15.1.3"),sQuery(id+"F5.wireOp",EDGE,"E15.1.4"),sQuery(id+"F5.wireOp",EDGE,"E15.1.5"),sQuery(id+"F5.wireOp",EDGE,"E15.1.6"),sQuery(id+"F5.wireOp",EDGE,"E15.2.0"),sQuery(id+"F5.wireOp",EDGE,"E15.2.1"),sQuery(id+"F5.wireOp",EDGE,"E15.2.2"),sQuery(id+"F5.wireOp",EDGE,"E15.2.3"),sQuery(id+"F5.wireOp",EDGE,"E15.2.4"),sQuery(id+"F5.wireOp",EDGE,"E15.2.5"),sQuery(id+"F5.wireOp",EDGE,"E15.2.6"),sQuery(id+"F5.wireOp",EDGE,"E15.3.0"),sQuery(id+"F5.wireOp",EDGE,"E15.3.1"),sQuery(id+"F5.wireOp",EDGE,"E15.3.2"),sQuery(id+"F5.wireOp",EDGE,"E15.3.3"),sQuery(id+"F5.wireOp",EDGE,"E15.3.4"),sQuery(id+"F5.wireOp",EDGE,"E15.3.5"),sQuery(id+"F5.wireOp",EDGE,"E15.3.6"),sQuery(id+"F5.wireOp",EDGE,"E15.4.0"),sQuery(id+"F5.wireOp",EDGE,"E15.4.1"),sQuery(id+"F5.wireOp",EDGE,"E15.4.2"),sQuery(id+"F5.wireOp",EDGE,"E15.4.3"),sQuery(id+"F5.wireOp",EDGE,"E15.4.4"),sQuery(id+"F5.wireOp",EDGE,"E15.4.5"),sQuery(id+"F5.wireOp",EDGE,"E15.4.6"),sQuery(id+"F5.wireOp",EDGE,"E15.5.0"),sQuery(id+"F5.wireOp",EDGE,"E15.5.1"),sQuery(id+"F5.wireOp",EDGE,"E15.5.2"),sQuery(id+"F5.wireOp",EDGE,"E15.5.3"),sQuery(id+"F5.wireOp",EDGE,"E15.5.4"),sQuery(id+"F5.wireOp",EDGE,"E15.5.5"),sQuery(id+"F5.wireOp",EDGE,"E15.5.6"),sQuery(id+"F5.wireOp",EDGE,"E15.6.0"),sQuery(id+"F5.wireOp",EDGE,"E15.6.1"),sQuery(id+"F5.wireOp",EDGE,"E15.6.2"),sQuery(id+"F5.wireOp",EDGE,"E15.6.3"),sQuery(id+"F5.wireOp",EDGE,"E15.6.4"),sQuery(id+"F5.wireOp",EDGE,"E15.6.5"),sQuery(id+"F5.wireOp",EDGE,"E15.6.6"),sQuery(id+"F5.wireOp",EDGE,"E15.7.0"),sQuery(id+"F5.wireOp",EDGE,"E15.7.1"),sQuery(id+"F5.wireOp",EDGE,"E15.7.2"),sQuery(id+"F5.wireOp",EDGE,"E15.7.3"),sQuery(id+"F5.wireOp",EDGE,"E15.7.4"),sQuery(id+"F5.wireOp",EDGE,"E15.7.5"),sQuery(id+"F5.wireOp",EDGE,"E15.7.6"),sQuery(id+"F5.wireOp",EDGE,"E15.8.0"),sQuery(id+"F5.wireOp",EDGE,"E15.8.1"),sQuery(id+"F5.wireOp",EDGE,"E15.8.2"),sQuery(id+"F5.wireOp",EDGE,"E15.8.3"),sQuery(id+"F5.wireOp",EDGE,"E15.8.4"),sQuery(id+"F5.wireOp",EDGE,"E15.8.5"),sQuery(id+"F5.wireOp",EDGE,"E15.8.6"),sQuery(id+"F5.wireOp",EDGE,"E15.9.0"),sQuery(id+"F5.wireOp",EDGE,"E15.9.1"),sQuery(id+"F5.wireOp",EDGE,"E15.9.2"),sQuery(id+"F5.wireOp",EDGE,"E15.9.3"),sQuery(id+"F5.wireOp",EDGE,"E15.9.4"),sQuery(id+"F5.wireOp",EDGE,"E15.9.5"),sQuery(id+"F5.wireOp",EDGE,"E15.9.6"),sQuery(id+"F5.wireOp",EDGE,"E15.10.0"),sQuery(id+"F5.wireOp",EDGE,"E15.10.1"),sQuery(id+"F5.wireOp",EDGE,"E15.10.2"),sQuery(id+"F5.wireOp",EDGE,"E15.10.3"),sQuery(id+"F5.wireOp",EDGE,"E15.10.4"),sQuery(id+"F5.wireOp",EDGE,"E15.10.5"),sQuery(id+"F5.wireOp",EDGE,"E15.10.6"),sQuery(id+"F5.wireOp",EDGE,"E15.11.0"),sQuery(id+"F5.wireOp",EDGE,"E15.11.1"),sQuery(id+"F5.wireOp",EDGE,"E15.11.2"),sQuery(id+"F5.wireOp",EDGE,"E15.11.3"),sQuery(id+"F5.wireOp",EDGE,"E15.11.4"),sQuery(id+"F5.wireOp",EDGE,"E15.11.5"),sQuery(id+"F5.wireOp",EDGE,"E15.11.6"),sQuery(id+"F5.wireOp",EDGE,"E15.12.0"),sQuery(id+"F5.wireOp",EDGE,"E15.12.1"),sQuery(id+"F5.wireOp",EDGE,"E15.12.2"),sQuery(id+"F5.wireOp",EDGE,"E15.12.3"),sQuery(id+"F5.wireOp",EDGE,"E15.12.4"),sQuery(id+"F5.wireOp",EDGE,"E15.12.5"),sQuery(id+"F5.wireOp",EDGE,"E15.12.6"),sQuery(id+"F5.wireOp",EDGE,"E15.13.0"),sQuery(id+"F5.wireOp",EDGE,"E15.13.1"),sQuery(id+"F5.wireOp",EDGE,"E15.13.2"),sQuery(id+"F5.wireOp",EDGE,"E15.13.3"),sQuery(id+"F5.wireOp",EDGE,"E15.13.4"),sQuery(id+"F5.wireOp",EDGE,"E15.13.5"),sQuery(id+"F5.wireOp",EDGE,"E15.13.6"),sQuery(id+"F5.wireOp",EDGE,"E15.14.0"),sQuery(id+"F5.wireOp",EDGE,"E15.14.1"),sQuery(id+"F5.wireOp",EDGE,"E15.14.2"),sQuery(id+"F5.wireOp",EDGE,"E15.14.3"),sQuery(id+"F5.wireOp",EDGE,"E15.14.4"),sQuery(id+"F5.wireOp",EDGE,"E15.14.5"),sQuery(id+"F5.wireOp",EDGE,"E15.14.6"),sQuery(id+"F5.wireOp",EDGE,"E15.15.0"),sQuery(id+"F5.wireOp",EDGE,"E15.15.1"),sQuery(id+"F5.wireOp",EDGE,"E15.15.2"),sQuery(id+"F5.wireOp",EDGE,"E15.15.3"),sQuery(id+"F5.wireOp",EDGE,"E15.15.4"),sQuery(id+"F5.wireOp",EDGE,"E15.15.5"),sQuery(id+"F5.wireOp",EDGE,"E15.15.6"),sQuery(id+"F5.wireOp",EDGE,"E15.16.0"),sQuery(id+"F5.wireOp",EDGE,"E15.16.1"),sQuery(id+"F5.wireOp",EDGE,"E15.16.2"),sQuery(id+"F5.wireOp",EDGE,"E15.16.3"),sQuery(id+"F5.wireOp",EDGE,"E15.16.4"),sQuery(id+"F5.wireOp",EDGE,"E15.16.5"),sQuery(id+"F5.wireOp",EDGE,"E15.16.6"),sQuery(id+"F5.wireOp",EDGE,"E15.17.0"),sQuery(id+"F5.wireOp",EDGE,"E15.17.1"),sQuery(id+"F5.wireOp",EDGE,"E15.17.2"),sQuery(id+"F5.wireOp",EDGE,"E15.17.3"),sQuery(id+"F5.wireOp",EDGE,"E15.17.4"),sQuery(id+"F5.wireOp",EDGE,"E15.17.5"),sQuery(id+"F5.wireOp",EDGE,"E15.17.6"),sQuery(id+"F5.wireOp",EDGE,"E15.18.0"),sQuery(id+"F5.wireOp",EDGE,"E15.18.1"),sQuery(id+"F5.wireOp",EDGE,"E15.18.2"),sQuery(id+"F5.wireOp",EDGE,"E15.18.3"),sQuery(id+"F5.wireOp",EDGE,"E15.18.4"),sQuery(id+"F5.wireOp",EDGE,"E15.18.5"),sQuery(id+"F5.wireOp",EDGE,"E15.18.6"),sQuery(id+"F5.wireOp",EDGE,"E15.19.0"),sQuery(id+"F5.wireOp",EDGE,"E15.19.1"),sQuery(id+"F5.wireOp",EDGE,"E15.19.2"),sQuery(id+"F5.wireOp",EDGE,"E15.19.3"),sQuery(id+"F5.wireOp",EDGE,"E15.19.4"),sQuery(id+"F5.wireOp",EDGE,"E15.19.5"),sQuery(id+"F5.wireOp",EDGE,"E15.19.6"),sQuery(id+"F5.wireOp",EDGE,"E15.20.0"),sQuery(id+"F5.wireOp",EDGE,"E15.20.1"),sQuery(id+"F5.wireOp",EDGE,"E15.20.2"),sQuery(id+"F5.wireOp",EDGE,"E15.20.3"),sQuery(id+"F5.wireOp",EDGE,"E15.20.4"),sQuery(id+"F5.wireOp",EDGE,"E15.20.5"),sQuery(id+"F5.wireOp",EDGE,"E15.20.6"),sQuery(id+"F5.wireOp",EDGE,"E15.21.0"),sQuery(id+"F5.wireOp",EDGE,"E15.21.1"),sQuery(id+"F5.wireOp",EDGE,"E15.21.2"),sQuery(id+"F5.wireOp",EDGE,"E15.21.3"),sQuery(id+"F5.wireOp",EDGE,"E15.21.4"),sQuery(id+"F5.wireOp",EDGE,"E15.21.5"),sQuery(id+"F5.wireOp",EDGE,"E15.21.6"),sQuery(id+"F5.wireOp",EDGE,"E15.22.0"),sQuery(id+"F5.wireOp",EDGE,"E15.22.1"),sQuery(id+"F5.wireOp",EDGE,"E15.22.2"),sQuery(id+"F5.wireOp",EDGE,"E15.22.3"),sQuery(id+"F5.wireOp",EDGE,"E15.22.4"),sQuery(id+"F5.wireOp",EDGE,"E15.22.5"),sQuery(id+"F5.wireOp",EDGE,"E15.22.6"),sQuery(id+"F5.wireOp",EDGE,"E15.23.0"),sQuery(id+"F5.wireOp",EDGE,"E15.23.1"),sQuery(id+"F5.wireOp",EDGE,"E15.23.2"),sQuery(id+"F5.wireOp",EDGE,"E15.23.3"),sQuery(id+"F5.wireOp",EDGE,"E15.23.4"),sQuery(id+"F5.wireOp",EDGE,"E15.23.5"),sQuery(id+"F5.wireOp",EDGE,"E15.23.6"),sQuery(id+"F5.wireOp",EDGE,"E15.24.0"),sQuery(id+"F5.wireOp",EDGE,"E15.24.1"),sQuery(id+"F5.wireOp",EDGE,"E15.24.2"),sQuery(id+"F5.wireOp",EDGE,"E15.24.3"),sQuery(id+"F5.wireOp",EDGE,"E15.24.4"),sQuery(id+"F5.wireOp",EDGE,"E15.24.5"),sQuery(id+"F5.wireOp",EDGE,"E15.24.6"),sQuery(id+"F5.wireOp",EDGE,"E15.25.0"),sQuery(id+"F5.wireOp",EDGE,"E15.25.1"),sQuery(id+"F5.wireOp",EDGE,"E15.25.2"),sQuery(id+"F5.wireOp",EDGE,"E15.25.3"),sQuery(id+"F5.wireOp",EDGE,"E15.25.4"),sQuery(id+"F5.wireOp",EDGE,"E15.25.5"),sQuery(id+"F5.wireOp",EDGE,"E15.25.6"),sQuery(id+"F5.wireOp",EDGE,"E15.26.0"),sQuery(id+"F5.wireOp",EDGE,"E15.26.1"),sQuery(id+"F5.wireOp",EDGE,"E15.26.2"),sQuery(id+"F5.wireOp",EDGE,"E15.26.3"),sQuery(id+"F5.wireOp",EDGE,"E15.26.4"),sQuery(id+"F5.wireOp",EDGE,"E15.26.5"),sQuery(id+"F5.wireOp",EDGE,"E15.26.6"),sQuery(id+"F5.wireOp",EDGE,"E15.27.0"),sQuery(id+"F5.wireOp",EDGE,"E15.27.1"),sQuery(id+"F5.wireOp",EDGE,"E15.27.2"),sQuery(id+"F5.wireOp",EDGE,"E15.27.3"),sQuery(id+"F5.wireOp",EDGE,"E15.27.4"),sQuery(id+"F5.wireOp",EDGE,"E15.27.5"),sQuery(id+"F5.wireOp",EDGE,"E15.27.6"),sQuery(id+"F5.wireOp",EDGE,"E15.28.0"),sQuery(id+"F5.wireOp",EDGE,"E15.28.1"),sQuery(id+"F5.wireOp",EDGE,"E15.28.2"),sQuery(id+"F5.wireOp",EDGE,"E15.28.3"),sQuery(id+"F5.wireOp",EDGE,"E15.28.4"),sQuery(id+"F5.wireOp",EDGE,"E15.28.5"),sQuery(id+"F5.wireOp",EDGE,"E15.28.6"),sQuery(id+"F5.wireOp",EDGE,"E15.29.0"),sQuery(id+"F5.wireOp",EDGE,"E15.29.1"),sQuery(id+"F5.wireOp",EDGE,"E15.29.2"),sQuery(id+"F5.wireOp",EDGE,"E15.29.3"),sQuery(id+"F5.wireOp",EDGE,"E15.29.4"),sQuery(id+"F5.wireOp",EDGE,"E15.29.5"),sQuery(id+"F5.wireOp",EDGE,"E15.29.6"),sQuery(id+"F5.wireOp",EDGE,"E15.30.0"),sQuery(id+"F5.wireOp",EDGE,"E15.30.1"),sQuery(id+"F5.wireOp",EDGE,"E15.30.2"),sQuery(id+"F5.wireOp",EDGE,"E15.30.3"),sQuery(id+"F5.wireOp",EDGE,"E15.30.4"),sQuery(id+"F5.wireOp",EDGE,"E15.30.5"),sQuery(id+"F5.wireOp",EDGE,"E15.30.6"),sQuery(id+"F5.wireOp",EDGE,"E15.31.0"),sQuery(id+"F5.wireOp",EDGE,"E15.31.1"),sQuery(id+"F5.wireOp",EDGE,"E15.31.2"),sQuery(id+"F5.wireOp",EDGE,"E15.31.3"),sQuery(id+"F5.wireOp",EDGE,"E15.31.4"),sQuery(id+"F5.wireOp",EDGE,"E15.31.5"),sQuery(id+"F5.wireOp",EDGE,"E15.31.6"),sQuery(id+"F5.wireOp",EDGE,"E15.32.0"),sQuery(id+"F5.wireOp",EDGE,"E15.32.1"),sQuery(id+"F5.wireOp",EDGE,"E15.32.2"),sQuery(id+"F5.wireOp",EDGE,"E15.32.3"),sQuery(id+"F5.wireOp",EDGE,"E15.32.4"),sQuery(id+"F5.wireOp",EDGE,"E15.32.5"),sQuery(id+"F5.wireOp",EDGE,"E15.32.6"),sQuery(id+"F5.wireOp",EDGE,"E15.33.0"),sQuery(id+"F5.wireOp",EDGE,"E15.33.1"),sQuery(id+"F5.wireOp",EDGE,"E15.33.2"),sQuery(id+"F5.wireOp",EDGE,"E15.33.3"),sQuery(id+"F5.wireOp",EDGE,"E15.33.4"),sQuery(id+"F5.wireOp",EDGE,"E15.33.5"),sQuery(id+"F5.wireOp",EDGE,"E15.33.6"),sQuery(id+"F5.wireOp",EDGE,"E15.34.0"),sQuery(id+"F5.wireOp",EDGE,"E15.34.1"),sQuery(id+"F5.wireOp",EDGE,"E15.34.2"),sQuery(id+"F5.wireOp",EDGE,"E15.34.3"),sQuery(id+"F5.wireOp",EDGE,"E15.34.4"),sQuery(id+"F5.wireOp",EDGE,"E15.34.5"),sQuery(id+"F5.wireOp",EDGE,"E15.34.6"),sQuery(id+"F5.wireOp",EDGE,"E15.35.0"),sQuery(id+"F5.wireOp",EDGE,"E15.35.1"),sQuery(id+"F5.wireOp",EDGE,"E15.35.2"),sQuery(id+"F5.wireOp",EDGE,"E15.35.3"),sQuery(id+"F5.wireOp",EDGE,"E15.35.4"),sQuery(id+"F5.wireOp",EDGE,"E15.35.5"),sQuery(id+"F5.wireOp",EDGE,"E15.35.6"),sQuery(id+"F5.wireOp",EDGE,"E15.36.0"),sQuery(id+"F5.wireOp",EDGE,"E15.36.1"),sQuery(id+"F5.wireOp",EDGE,"E15.36.2"),sQuery(id+"F5.wireOp",EDGE,"E15.36.3"),sQuery(id+"F5.wireOp",EDGE,"E15.36.4"),sQuery(id+"F5.wireOp",EDGE,"E15.36.5"),sQuery(id+"F5.wireOp",EDGE,"E15.36.6"),sQuery(id+"F5.wireOp",EDGE,"E15.37.0"),sQuery(id+"F5.wireOp",EDGE,"E15.37.1"),sQuery(id+"F5.wireOp",EDGE,"E15.37.2"),sQuery(id+"F5.wireOp",EDGE,"E15.37.3"),sQuery(id+"F5.wireOp",EDGE,"E15.37.4"),sQuery(id+"F5.wireOp",EDGE,"E15.37.5"),sQuery(id+"F5.wireOp",EDGE,"E15.37.6"),sQuery(id+"F5.wireOp",EDGE,"E15.38.0"),sQuery(id+"F5.wireOp",EDGE,"E15.38.1"),sQuery(id+"F5.wireOp",EDGE,"E15.38.2"),sQuery(id+"F5.wireOp",EDGE,"E15.38.3"),sQuery(id+"F5.wireOp",EDGE,"E15.38.4"),sQuery(id+"F5.wireOp",EDGE,"E15.38.5"),sQuery(id+"F5.wireOp",EDGE,"E15.38.6"),sQuery(id+"F5.wireOp",EDGE,"E15.39.0"),sQuery(id+"F5.wireOp",EDGE,"E15.39.1"),sQuery(id+"F5.wireOp",EDGE,"E15.39.2"),sQuery(id+"F5.wireOp",EDGE,"E15.39.3"),sQuery(id+"F5.wireOp",EDGE,"E15.39.4"),sQuery(id+"F5.wireOp",EDGE,"E15.39.5"),sQuery(id+"F5.wireOp",EDGE,"E15.39.6"),sQuery(id+"F5.wireOp",EDGE,"E15.40.0"),sQuery(id+"F5.wireOp",EDGE,"E15.40.1"),sQuery(id+"F5.wireOp",EDGE,"E15.40.2"),sQuery(id+"F5.wireOp",EDGE,"E15.40.3"),sQuery(id+"F5.wireOp",EDGE,"E15.40.4"),sQuery(id+"F5.wireOp",EDGE,"E15.40.5"),sQuery(id+"F5.wireOp",EDGE,"E15.40.6"),sQuery(id+"F5.wireOp",EDGE,"E15.41.0"),sQuery(id+"F5.wireOp",EDGE,"E15.41.1"),sQuery(id+"F5.wireOp",EDGE,"E15.41.2"),sQuery(id+"F5.wireOp",EDGE,"E15.41.3"),sQuery(id+"F5.wireOp",EDGE,"E15.41.4"),sQuery(id+"F5.wireOp",EDGE,"E15.41.5"),sQuery(id+"F5.wireOp",EDGE,"E15.41.6"),sQuery(id+"F5.wireOp",EDGE,"E15.42.0"),sQuery(id+"F5.wireOp",EDGE,"E15.42.1"),sQuery(id+"F5.wireOp",EDGE,"E15.42.2"),sQuery(id+"F5.wireOp",EDGE,"E15.42.3"),sQuery(id+"F5.wireOp",EDGE,"E15.42.4"),sQuery(id+"F5.wireOp",EDGE,"E15.42.5"),sQuery(id+"F5.wireOp",EDGE,"E15.42.6")])],"isStart":false});
            var sketch = newSketch(context, id + "F7", { "sketchPlane" : qUnion([Q0])});
            skCircle(sketch, "E16", {"center": v(0, 0) * mm, "radius": 8.85 * mm});
            skSolve(sketch);
        }
        {
            var Q0;
            Q0=makeQuery(id+"F7.imprint","IMPRINT",FACE,{"disambiguationData":[TD([[makeQuery(id+"F7.imprint","IMPRINT",EDGE,{"derivedFrom":sQuery(id+"F7.wireOp",EDGE,"E16")}),1.0]])]});
            extrude(context, id + "F8", {"entities" : qUnion([Q0]), "operationType" : NewBodyOperationType.ADD, "depth" : 5.2 * mm, "offsetDistance" : 25 * mm});
        }
        {
            var Q0;
            Q0=makeQuery(id+"F8.opExtrude","CAP_FACE",FACE,{"disambiguationData":[OSD([sQuery(id+"F0.wireOp",EDGE,"E1.0"),sQuery(id+"F0.wireOp",EDGE,"E1.1"),sQuery(id+"F0.wireOp",EDGE,"E1.2"),sQuery(id+"F0.wireOp",EDGE,"E1.3"),sQuery(id+"F0.wireOp",EDGE,"E1.4"),sQuery(id+"F0.wireOp",EDGE,"E1.5"),sQuery(id+"F7.wireOp",EDGE,"E16")])],"isStart":false});
            var sketch = newSketch(context, id + "F9", { "sketchPlane" : qUnion([Q0])});
            skCircle(sketch, "E17", {"center": v(0, 0) * mm, "radius": 7.8 * mm});
            skSolve(sketch);
        }
        {
            var Q0;
            Q0=makeQuery(id+"F9.imprint","IMPRINT",FACE,{"disambiguationData":[TD([[makeQuery(id+"F9.imprint","IMPRINT",EDGE,{"derivedFrom":sQuery(id+"F9.wireOp",EDGE,"E17")}),1.0]])]});
            extrude(context, id + "F10", {"entities" : qUnion([Q0]), "operationType" : NewBodyOperationType.ADD, "depth" : 7 * mm, "offsetDistance" : 25 * mm});
        }
        {
            var Q0;
            Q0=makeQuery(id+"F1.opExtrude","CAP_FACE",FACE,{"disambiguationData":[OSD([sQuery(id+"F0.wireOp",EDGE,"E0"),sQuery(id+"F0.wireOp",EDGE,"E2")])],"isStart":false});
            var sketch = newSketch(context, id + "F11", { "sketchPlane" : qUnion([Q0])});
            skCircle(sketch, "E18", {"center": v(0, 0) * mm, "radius": 4.9 * mm, "construction": true});
            skLineSegment(sketch, "E19", {"start": v(0, 0) * mm, "end": v(0, 6.9) * mm, "construction": true});
            skCircle(sketch, "E20", {"center": v(0, 0) * mm, "radius": 3.9 * mm, "construction": true});
            skCircle(sketch, "E21", {"center": v(0, 0) * mm, "radius": 6.9 * mm, "construction": true});
            skArc(sketch, "E22", {"start": v(-1.19, 4.75) * mm, "mid": v(-1.7, 3.51) * mm, "end": v(-2.98, 3.9) * mm});
            skArc(sketch, "E23", {"start": v(-0.5, 6.88) * mm, "mid": v(-0.25, 6.9) * mm, "end": v(0, 6.9) * mm});
            skLineSegment(sketch, "E24", {"start": v(-1.19, 4.75) * mm, "end": v(-1.36, 5.22) * mm});
            skLineSegment(sketch, "E25", {"start": v(-1.36, 5.22) * mm, "end": v(-0.5, 6.88) * mm});
            skArc(sketch, "E26.MirrorCS", {"start": v(0.5, 6.88) * mm, "mid": v(0.25, 6.9) * mm, "end": v(0, 6.9) * mm});
            skLineSegment(sketch, "E27.MirrorCS", {"start": v(1.36, 5.22) * mm, "end": v(0.5, 6.88) * mm});
            skLineSegment(sketch, "E28.MirrorCS", {"start": v(1.19, 4.75) * mm, "end": v(1.36, 5.22) * mm});
            skPoint(sketch, "E29.center", {"position": v(0, -0.03) * mm});
            skPoint(sketch, "E30.1.0", {"position": v(0.02, -0.02) * mm});
            skArc(sketch, "E30.1.1", {"start": v(-5.07, 4.68) * mm, "mid": v(-5.24, 4.5) * mm, "end": v(-5.4, 4.3) * mm});
            skArc(sketch, "E30.1.2", {"start": v(-5.7, 3.9) * mm, "mid": v(-5.55, 4.1) * mm, "end": v(-5.4, 4.3) * mm});
            skLineSegment(sketch, "E30.1.3", {"start": v(-3.24, 4.32) * mm, "end": v(-5.07, 4.68) * mm});
            skLineSegment(sketch, "E30.1.4", {"start": v(-2.98, 3.9) * mm, "end": v(-3.24, 4.32) * mm});
            skLineSegment(sketch, "E30.1.5", {"start": v(-4.93, 2.2) * mm, "end": v(-5.7, 3.9) * mm});
            skLineSegment(sketch, "E30.1.6", {"start": v(-4.46, 2.04) * mm, "end": v(-4.93, 2.2) * mm});
            skArc(sketch, "E30.1.7", {"start": v(-4.46, 2.04) * mm, "mid": v(-3.8, 0.87) * mm, "end": v(-4.9, 0.1) * mm});
            skPoint(sketch, "E30.2.0", {"position": v(0.03, 0) * mm});
            skArc(sketch, "E30.2.1", {"start": v(-6.82, -1.04) * mm, "mid": v(-6.78, -1.3) * mm, "end": v(-6.73, -1.54) * mm});
            skArc(sketch, "E30.2.2", {"start": v(-6.6, -2.02) * mm, "mid": v(-6.67, -1.78) * mm, "end": v(-6.73, -1.54) * mm});
            skLineSegment(sketch, "E30.2.3", {"start": v(-5.4, 0.16) * mm, "end": v(-6.82, -1.04) * mm});
            skLineSegment(sketch, "E30.2.4", {"start": v(-4.9, 0.1) * mm, "end": v(-5.4, 0.16) * mm});
            skLineSegment(sketch, "E30.2.5", {"start": v(-4.8, -2.48) * mm, "end": v(-6.6, -2.02) * mm});
            skLineSegment(sketch, "E30.2.6", {"start": v(-4.37, -2.21) * mm, "end": v(-4.8, -2.48) * mm});
            skArc(sketch, "E30.2.7", {"start": v(-4.37, -2.21) * mm, "mid": v(-3.05, -2.43) * mm, "end": v(-3.13, -3.77) * mm});
            skPoint(sketch, "E30.3.0", {"position": v(0.01, 0.02) * mm});
            skArc(sketch, "E30.3.1", {"start": v(-3.44, -5.98) * mm, "mid": v(-3.22, -6.1) * mm, "end": v(-3, -6.22) * mm});
            skArc(sketch, "E30.3.2", {"start": v(-2.54, -6.42) * mm, "mid": v(-2.77, -6.32) * mm, "end": v(-3, -6.22) * mm});
            skLineSegment(sketch, "E30.3.3", {"start": v(-3.49, -4.12) * mm, "end": v(-3.44, -5.98) * mm});
            skLineSegment(sketch, "E30.3.4", {"start": v(-3.13, -3.77) * mm, "end": v(-3.49, -4.12) * mm});
            skLineSegment(sketch, "E30.3.5", {"start": v(-1.05, -5.3) * mm, "end": v(-2.54, -6.42) * mm});
            skLineSegment(sketch, "E30.3.6", {"start": v(-1, -4.8) * mm, "end": v(-1.05, -5.3) * mm});
            skArc(sketch, "E30.3.7", {"start": v(-1, -4.8) * mm, "mid": v(0, -3.9) * mm, "end": v(1, -4.8) * mm});
            skPoint(sketch, "E30.4.0", {"position": v(-0.01, 0.02) * mm});
            skArc(sketch, "E30.4.1", {"start": v(2.54, -6.42) * mm, "mid": v(2.77, -6.32) * mm, "end": v(3, -6.22) * mm});
            skArc(sketch, "E30.4.2", {"start": v(3.44, -5.98) * mm, "mid": v(3.22, -6.1) * mm, "end": v(3, -6.22) * mm});
            skLineSegment(sketch, "E30.4.3", {"start": v(1.05, -5.3) * mm, "end": v(2.54, -6.42) * mm});
            skLineSegment(sketch, "E30.4.4", {"start": v(1, -4.8) * mm, "end": v(1.05, -5.3) * mm});
            skLineSegment(sketch, "E30.4.5", {"start": v(3.49, -4.12) * mm, "end": v(3.44, -5.98) * mm});
            skLineSegment(sketch, "E30.4.6", {"start": v(3.13, -3.77) * mm, "end": v(3.49, -4.12) * mm});
            skArc(sketch, "E30.4.7", {"start": v(3.13, -3.77) * mm, "mid": v(3.05, -2.43) * mm, "end": v(4.37, -2.21) * mm});
            skPoint(sketch, "E30.5.0", {"position": v(-0.03, 0) * mm});
            skArc(sketch, "E30.5.1", {"start": v(6.6, -2.02) * mm, "mid": v(6.67, -1.78) * mm, "end": v(6.73, -1.54) * mm});
            skArc(sketch, "E30.5.2", {"start": v(6.82, -1.04) * mm, "mid": v(6.78, -1.3) * mm, "end": v(6.73, -1.54) * mm});
            skLineSegment(sketch, "E30.5.3", {"start": v(4.8, -2.48) * mm, "end": v(6.6, -2.02) * mm});
            skLineSegment(sketch, "E30.5.4", {"start": v(4.37, -2.21) * mm, "end": v(4.8, -2.48) * mm});
            skLineSegment(sketch, "E30.5.5", {"start": v(5.4, 0.16) * mm, "end": v(6.82, -1.04) * mm});
            skLineSegment(sketch, "E30.5.6", {"start": v(4.9, 0.1) * mm, "end": v(5.4, 0.16) * mm});
            skArc(sketch, "E30.5.7", {"start": v(4.9, 0.1) * mm, "mid": v(3.8, 0.87) * mm, "end": v(4.46, 2.04) * mm});
            skPoint(sketch, "E30.6.0", {"position": v(-0.02, -0.02) * mm});
            skArc(sketch, "E30.6.1", {"start": v(5.7, 3.9) * mm, "mid": v(5.55, 4.1) * mm, "end": v(5.4, 4.3) * mm});
            skArc(sketch, "E30.6.2", {"start": v(5.07, 4.68) * mm, "mid": v(5.24, 4.5) * mm, "end": v(5.4, 4.3) * mm});
            skLineSegment(sketch, "E30.6.3", {"start": v(4.93, 2.2) * mm, "end": v(5.7, 3.9) * mm});
            skLineSegment(sketch, "E30.6.4", {"start": v(4.46, 2.04) * mm, "end": v(4.93, 2.2) * mm});
            skLineSegment(sketch, "E30.6.5", {"start": v(3.24, 4.32) * mm, "end": v(5.07, 4.68) * mm});
            skLineSegment(sketch, "E30.6.6", {"start": v(2.98, 3.9) * mm, "end": v(3.24, 4.32) * mm});
            skArc(sketch, "E30.6.7", {"start": v(2.98, 3.9) * mm, "mid": v(1.7, 3.51) * mm, "end": v(1.19, 4.75) * mm});
            skSolve(sketch);
        }
        {
            var Q0;
            Q0=makeQuery(id+"F11.imprint","IMPRINT",FACE,{"disambiguationData":[TD([[makeQuery(id+"F11.imprint","IMPRINT",EDGE,{"derivedFrom":sQuery(id+"F11.wireOp",EDGE,"E22")}),1.0]])]});
            extrude(context, id + "F12", {"entities" : qUnion([Q0]), "operationType" : NewBodyOperationType.ADD, "depth" : 8.8 * mm, "offsetDistance" : 25 * mm});
        }
        {
            var Q0;
            Q0=makeQuery(id+"F12.opExtrude","CAP_FACE",FACE,{"disambiguationData":[OSD([sQuery(id+"F0.wireOp",EDGE,"E2"),sQuery(id+"F11.wireOp",EDGE,"E22"),sQuery(id+"F11.wireOp",EDGE,"E23"),sQuery(id+"F11.wireOp",EDGE,"E24"),sQuery(id+"F11.wireOp",EDGE,"E25"),sQuery(id+"F11.wireOp",EDGE,"E26.MirrorCS"),sQuery(id+"F11.wireOp",EDGE,"E27.MirrorCS"),sQuery(id+"F11.wireOp",EDGE,"E28.MirrorCS"),sQuery(id+"F11.wireOp",EDGE,"E30.1.1"),sQuery(id+"F11.wireOp",EDGE,"E30.1.2"),sQuery(id+"F11.wireOp",EDGE,"E30.1.3"),sQuery(id+"F11.wireOp",EDGE,"E30.1.4"),sQuery(id+"F11.wireOp",EDGE,"E30.1.5"),sQuery(id+"F11.wireOp",EDGE,"E30.1.6"),sQuery(id+"F11.wireOp",EDGE,"E30.1.7"),sQuery(id+"F11.wireOp",EDGE,"E30.2.1"),sQuery(id+"F11.wireOp",EDGE,"E30.2.2"),sQuery(id+"F11.wireOp",EDGE,"E30.2.3"),sQuery(id+"F11.wireOp",EDGE,"E30.2.4"),sQuery(id+"F11.wireOp",EDGE,"E30.2.5"),sQuery(id+"F11.wireOp",EDGE,"E30.2.6"),sQuery(id+"F11.wireOp",EDGE,"E30.2.7"),sQuery(id+"F11.wireOp",EDGE,"E30.3.1"),sQuery(id+"F11.wireOp",EDGE,"E30.3.2"),sQuery(id+"F11.wireOp",EDGE,"E30.3.3"),sQuery(id+"F11.wireOp",EDGE,"E30.3.4"),sQuery(id+"F11.wireOp",EDGE,"E30.3.5"),sQuery(id+"F11.wireOp",EDGE,"E30.3.6"),sQuery(id+"F11.wireOp",EDGE,"E30.3.7"),sQuery(id+"F11.wireOp",EDGE,"E30.4.1"),sQuery(id+"F11.wireOp",EDGE,"E30.4.2"),sQuery(id+"F11.wireOp",EDGE,"E30.4.3"),sQuery(id+"F11.wireOp",EDGE,"E30.4.4"),sQuery(id+"F11.wireOp",EDGE,"E30.4.5"),sQuery(id+"F11.wireOp",EDGE,"E30.4.6"),sQuery(id+"F11.wireOp",EDGE,"E30.4.7"),sQuery(id+"F11.wireOp",EDGE,"E30.5.1"),sQuery(id+"F11.wireOp",EDGE,"E30.5.2"),sQuery(id+"F11.wireOp",EDGE,"E30.5.3"),sQuery(id+"F11.wireOp",EDGE,"E30.5.4"),sQuery(id+"F11.wireOp",EDGE,"E30.5.5"),sQuery(id+"F11.wireOp",EDGE,"E30.5.6"),sQuery(id+"F11.wireOp",EDGE,"E30.5.7"),sQuery(id+"F11.wireOp",EDGE,"E30.6.1"),sQuery(id+"F11.wireOp",EDGE,"E30.6.2"),sQuery(id+"F11.wireOp",EDGE,"E30.6.3"),sQuery(id+"F11.wireOp",EDGE,"E30.6.4"),sQuery(id+"F11.wireOp",EDGE,"E30.6.5"),sQuery(id+"F11.wireOp",EDGE,"E30.6.6"),sQuery(id+"F11.wireOp",EDGE,"E30.6.7")])],"isStart":false});
            var sketch = newSketch(context, id + "F13", { "sketchPlane" : qUnion([Q0])});
            skCircle(sketch, "E31", {"center": v(0, 0) * mm, "radius": 2.98 * mm});
            skSolve(sketch);
        }
        {
            var Q0;
            Q0=makeQuery(id+"F13.imprint","IMPRINT",FACE,{"disambiguationData":[TD([[makeQuery(id+"F13.imprint","IMPRINT",EDGE,{"derivedFrom":sQuery(id+"F13.wireOp",EDGE,"E31")}),1.0]])]});
            extrude(context, id + "F14", {"entities" : qUnion([Q0]), "operationType" : NewBodyOperationType.ADD, "depth" : 5.35 * mm, "offsetDistance" : 25 * mm});
        }
        {
            var Q0;
            Q0=makeQuery(id+"F14.opExtrude","CAP_EDGE",EDGE,{"disambiguationData":[OSD([sQuery(id+"F13.wireOp",EDGE,"E31")])],"isStart":false});
            var Q1;
            Q1=makeQuery(id+"F1.opExtrude","CAP_EDGE",EDGE,{"disambiguationData":[OSD([sQuery(id+"F0.wireOp",EDGE,"E0")])],"isStart":false});
            var Q2;
            Q2=makeQuery(id+"F10.opExtrude","CAP_EDGE",EDGE,{"disambiguationData":[OSD([sQuery(id+"F9.wireOp",EDGE,"E17")])],"isStart":false});
            chamfer(context, id + "F15", {"entities" : qUnion([Q0, Q1, Q2]), "width" : 0.3 * mm, "tangentPropagation" : true});
        }
        {
            var Q0;
            Q0=makeQuery(id+"F12.opExtrude","SWEPT_EDGE",EDGE,{"disambiguationData":[OSD([sQuery(id+"F11.wireOp",EDGE,"E24"),sQuery(id+"F11.wireOp",EDGE,"E25")])]});
            var Q1;
            Q1=makeQuery(id+"F12.opExtrude","SWEPT_EDGE",EDGE,{"disambiguationData":[OSD([sQuery(id+"F11.wireOp",EDGE,"E30.1.5"),sQuery(id+"F11.wireOp",EDGE,"E30.1.6")])]});
            var Q2;
            Q2=makeQuery(id+"F12.opExtrude","SWEPT_EDGE",EDGE,{"disambiguationData":[OSD([sQuery(id+"F11.wireOp",EDGE,"E30.2.5"),sQuery(id+"F11.wireOp",EDGE,"E30.2.6")])]});
            var Q3;
            Q3=makeQuery(id+"F12.opExtrude","SWEPT_EDGE",EDGE,{"disambiguationData":[OSD([sQuery(id+"F11.wireOp",EDGE,"E30.3.5"),sQuery(id+"F11.wireOp",EDGE,"E30.3.6")])]});
            var Q4;
            Q4=makeQuery(id+"F12.opExtrude","SWEPT_EDGE",EDGE,{"disambiguationData":[OSD([sQuery(id+"F11.wireOp",EDGE,"E30.4.5"),sQuery(id+"F11.wireOp",EDGE,"E30.4.6")])]});
            var Q5;
            Q5=makeQuery(id+"F12.opExtrude","SWEPT_EDGE",EDGE,{"disambiguationData":[OSD([sQuery(id+"F11.wireOp",EDGE,"E30.5.5"),sQuery(id+"F11.wireOp",EDGE,"E30.5.6")])]});
            var Q6;
            Q6=makeQuery(id+"F12.opExtrude","SWEPT_EDGE",EDGE,{"disambiguationData":[OSD([sQuery(id+"F11.wireOp",EDGE,"E30.6.5"),sQuery(id+"F11.wireOp",EDGE,"E30.6.6")])]});
            var Q7;
            Q7=makeQuery(id+"F12.opExtrude","SWEPT_EDGE",EDGE,{"disambiguationData":[OSD([sQuery(id+"F11.wireOp",EDGE,"E30.5.3"),sQuery(id+"F11.wireOp",EDGE,"E30.5.4")])]});
            var Q8;
            Q8=makeQuery(id+"F12.opExtrude","SWEPT_EDGE",EDGE,{"disambiguationData":[OSD([sQuery(id+"F11.wireOp",EDGE,"E30.4.3"),sQuery(id+"F11.wireOp",EDGE,"E30.4.4")])]});
            var Q9;
            Q9=makeQuery(id+"F12.opExtrude","SWEPT_EDGE",EDGE,{"disambiguationData":[OSD([sQuery(id+"F11.wireOp",EDGE,"E30.3.3"),sQuery(id+"F11.wireOp",EDGE,"E30.3.4")])]});
            var Q10;
            Q10=makeQuery(id+"F12.opExtrude","SWEPT_EDGE",EDGE,{"disambiguationData":[OSD([sQuery(id+"F11.wireOp",EDGE,"E30.2.3"),sQuery(id+"F11.wireOp",EDGE,"E30.2.4")])]});
            var Q11;
            Q11=makeQuery(id+"F12.opExtrude","SWEPT_EDGE",EDGE,{"disambiguationData":[OSD([sQuery(id+"F11.wireOp",EDGE,"E30.1.3"),sQuery(id+"F11.wireOp",EDGE,"E30.1.4")])]});
            var Q12;
            Q12=makeQuery(id+"F12.opExtrude","SWEPT_EDGE",EDGE,{"disambiguationData":[OSD([sQuery(id+"F11.wireOp",EDGE,"E27.MirrorCS"),sQuery(id+"F11.wireOp",EDGE,"E28.MirrorCS")])]});
            var Q13;
            Q13=makeQuery(id+"F12.opExtrude","SWEPT_EDGE",EDGE,{"disambiguationData":[OSD([sQuery(id+"F11.wireOp",EDGE,"E30.6.3"),sQuery(id+"F11.wireOp",EDGE,"E30.6.4")])]});
            fillet(context, id + "F16", {"entities" : qUnion([Q0, Q1, Q2, Q3, Q4, Q5, Q6, Q7, Q8, Q9, Q10, Q11, Q12, Q13]), "radius" : 1 * mm, "tangentPropagation" : true, "allowEdgeOverflow" : false});
        }
        {
            var Q0;
            Q0=makeQuery(id+"F12.opExtrude","SWEPT_EDGE",EDGE,{"disambiguationData":[OSD([sQuery(id+"F11.wireOp",EDGE,"E23"),sQuery(id+"F11.wireOp",EDGE,"E25")])]});
            var Q1;
            Q1=makeQuery(id+"F12.opExtrude","SWEPT_EDGE",EDGE,{"disambiguationData":[OSD([sQuery(id+"F11.wireOp",EDGE,"E30.1.2"),sQuery(id+"F11.wireOp",EDGE,"E30.1.5")])]});
            var Q2;
            Q2=makeQuery(id+"F12.opExtrude","SWEPT_EDGE",EDGE,{"disambiguationData":[OSD([sQuery(id+"F11.wireOp",EDGE,"E26.MirrorCS"),sQuery(id+"F11.wireOp",EDGE,"E27.MirrorCS")])]});
            var Q3;
            Q3=makeQuery(id+"F12.opExtrude","SWEPT_EDGE",EDGE,{"disambiguationData":[OSD([sQuery(id+"F11.wireOp",EDGE,"E30.2.2"),sQuery(id+"F11.wireOp",EDGE,"E30.2.5")])]});
            var Q4;
            Q4=makeQuery(id+"F12.opExtrude","SWEPT_EDGE",EDGE,{"disambiguationData":[OSD([sQuery(id+"F11.wireOp",EDGE,"E30.3.2"),sQuery(id+"F11.wireOp",EDGE,"E30.3.5")])]});
            var Q5;
            Q5=makeQuery(id+"F12.opExtrude","SWEPT_EDGE",EDGE,{"disambiguationData":[OSD([sQuery(id+"F11.wireOp",EDGE,"E30.4.2"),sQuery(id+"F11.wireOp",EDGE,"E30.4.5")])]});
            var Q6;
            Q6=makeQuery(id+"F12.opExtrude","SWEPT_EDGE",EDGE,{"disambiguationData":[OSD([sQuery(id+"F11.wireOp",EDGE,"E30.5.2"),sQuery(id+"F11.wireOp",EDGE,"E30.5.5")])]});
            var Q7;
            Q7=makeQuery(id+"F12.opExtrude","SWEPT_EDGE",EDGE,{"disambiguationData":[OSD([sQuery(id+"F11.wireOp",EDGE,"E30.6.2"),sQuery(id+"F11.wireOp",EDGE,"E30.6.5")])]});
            chamfer(context, id + "F17", {"entities" : qUnion([Q0, Q1, Q2, Q3, Q4, Q5, Q6, Q7]), "chamferType" : ChamferType.TWO_OFFSETS, "width1" : 0.9 * mm, "oppositeDirection" : false, "width2" : 0.15 * mm, "tangentPropagation" : true});
        }
        {
            var Q0;
            Q0=makeQuery(id+"F12.opExtrude","SWEPT_EDGE",EDGE,{"disambiguationData":[OSD([sQuery(id+"F11.wireOp",EDGE,"E30.6.1"),sQuery(id+"F11.wireOp",EDGE,"E30.6.3")])]});
            var Q1;
            Q1=makeQuery(id+"F12.opExtrude","SWEPT_EDGE",EDGE,{"disambiguationData":[OSD([sQuery(id+"F11.wireOp",EDGE,"E30.5.1"),sQuery(id+"F11.wireOp",EDGE,"E30.5.3")])]});
            var Q2;
            Q2=makeQuery(id+"F12.opExtrude","SWEPT_EDGE",EDGE,{"disambiguationData":[OSD([sQuery(id+"F11.wireOp",EDGE,"E30.4.1"),sQuery(id+"F11.wireOp",EDGE,"E30.4.3")])]});
            var Q3;
            Q3=makeQuery(id+"F12.opExtrude","SWEPT_EDGE",EDGE,{"disambiguationData":[OSD([sQuery(id+"F11.wireOp",EDGE,"E30.3.1"),sQuery(id+"F11.wireOp",EDGE,"E30.3.3")])]});
            var Q4;
            Q4=makeQuery(id+"F12.opExtrude","SWEPT_EDGE",EDGE,{"disambiguationData":[OSD([sQuery(id+"F11.wireOp",EDGE,"E30.1.1"),sQuery(id+"F11.wireOp",EDGE,"E30.1.3")])]});
            var Q5;
            Q5=makeQuery(id+"F12.opExtrude","SWEPT_EDGE",EDGE,{"disambiguationData":[OSD([sQuery(id+"F11.wireOp",EDGE,"E30.2.1"),sQuery(id+"F11.wireOp",EDGE,"E30.2.3")])]});
            chamfer(context, id + "F18", {"entities" : qUnion([Q0, Q1, Q2, Q3, Q4, Q5]), "chamferType" : ChamferType.TWO_OFFSETS, "width1" : 0.15 * mm, "oppositeDirection" : false, "width2" : 0.9 * mm, "tangentPropagation" : true});
        }
        {
            var Q0;
            Q0=makeQuery(id+"F10.opExtrude","CAP_FACE",FACE,{"disambiguationData":[OSD([sQuery(id+"F0.wireOp",EDGE,"E1.0"),sQuery(id+"F0.wireOp",EDGE,"E1.1"),sQuery(id+"F0.wireOp",EDGE,"E1.2"),sQuery(id+"F0.wireOp",EDGE,"E1.3"),sQuery(id+"F0.wireOp",EDGE,"E1.4"),sQuery(id+"F0.wireOp",EDGE,"E1.5"),sQuery(id+"F9.wireOp",EDGE,"E17")])],"isStart":false});
            var sketch = newSketch(context, id + "F19", { "sketchPlane" : qUnion([Q0])});
            skLineSegment(sketch, "E32.bottom", {"start": v(-0.5, -7.25) * mm, "end": v(0.5, -7.25) * mm});
            skLineSegment(sketch, "E32.top", {"start": v(-0.5, -11.6) * mm, "end": v(0.5, -11.6) * mm});
            skLineSegment(sketch, "E32.left", {"start": v(-0.5, -7.25) * mm, "end": v(-0.5, -11.6) * mm});
            skLineSegment(sketch, "E32.right", {"start": v(0.5, -7.25) * mm, "end": v(0.5, -11.6) * mm});
            skPoint(sketch, "E32.middle", {"position": v(0, -9.42) * mm});
            skSolve(sketch);
        }
        {
            var Q0;
            {var subQ0=sQuery(id+"F19.wireOp",EDGE,"E32.bottom");Q0=makeQuery(id+"F19.imprint","IMPRINT",FACE,{"disambiguationData":[TD([[makeQuery(id+"F19.imprint","IMPRINT",EDGE,{"derivedFrom":subQ0}),-1.0]])]});}
            var Q1;
            {var subQ0=sQuery(id+"F19.wireOp",EDGE,"E32.top");Q1=makeQuery(id+"F19.imprint","IMPRINT",FACE,{"disambiguationData":[TD([[makeQuery(id+"F19.imprint","IMPRINT",EDGE,{"derivedFrom":subQ0}),1.0]])]});}
            extrude(context, id + "F20", {"entities" : qUnion([Q0, Q1]), "operationType" : NewBodyOperationType.REMOVE, "oppositeDirection" : true, "depth" : 6 * mm, "offsetDistance" : 25 * mm});
        }
    });
